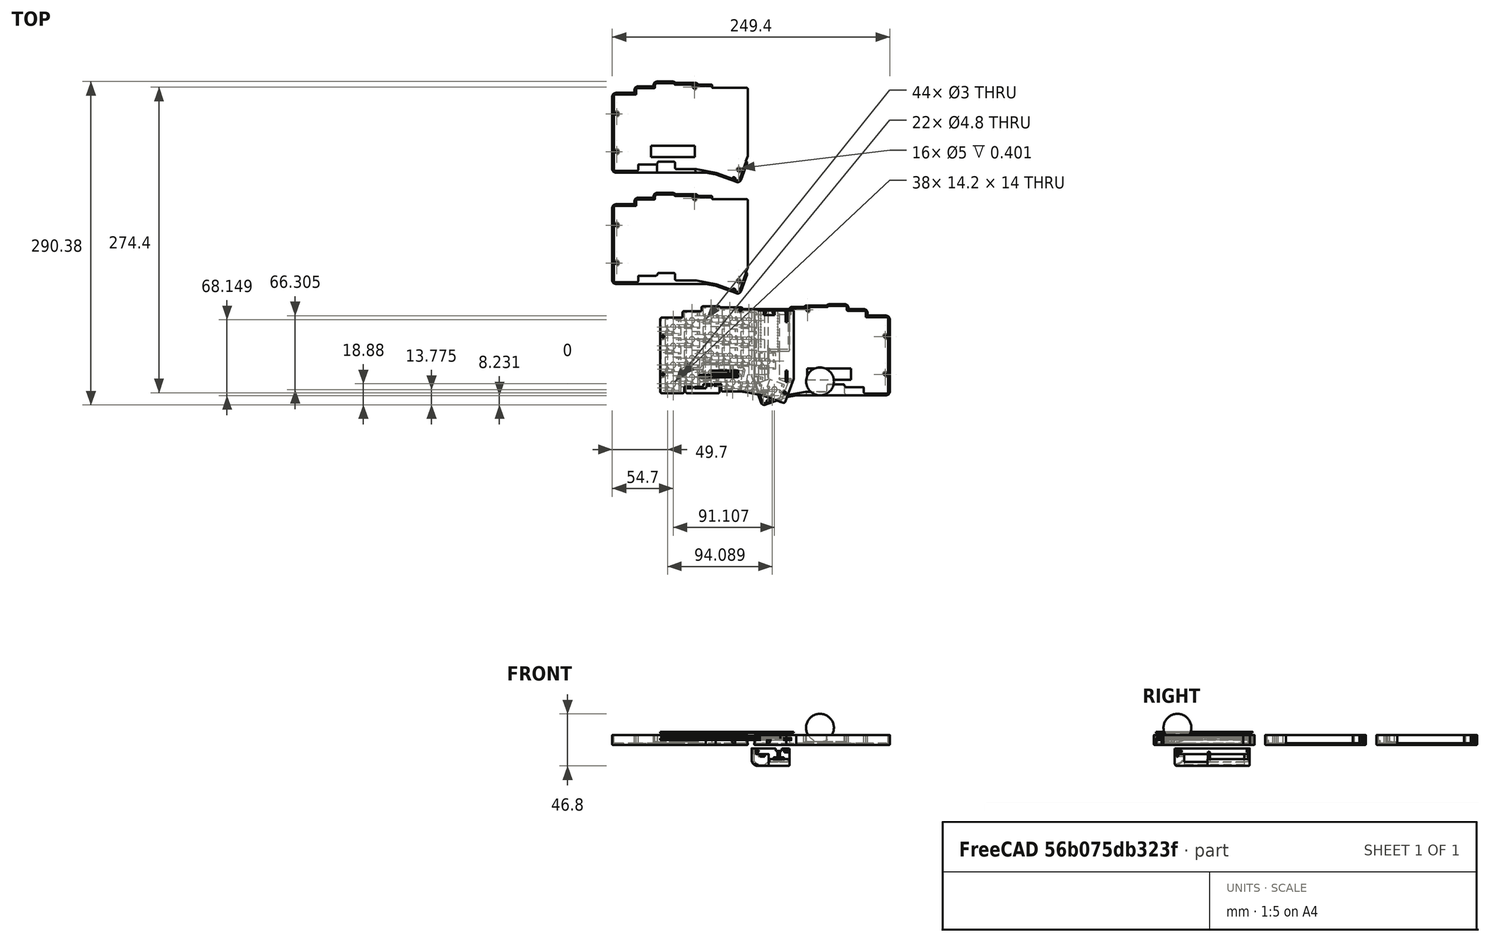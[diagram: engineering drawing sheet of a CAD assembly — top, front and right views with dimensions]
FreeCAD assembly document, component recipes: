
FREECAD ASSEMBLY — COMPONENT RECIPES ("simple-case-xs")

This assembly document has 5 components, labeled P0..P4 below (a component is one placed body or linked part). 4 of them carry a construction recipe — the FreeCAD feature program that regenerates the part from scratch, quoted from this document or its linked companion documents; the rest are supplied as boundary geometry only. No exploded tour is included for this assembly.
NOTE — this tour is split across 3 documents so each fits a 32k-token context. This is document 1: the component sections continue in the remaining 2 documents, each repeating the header above.
COMPONENT P0 — recipe-attached ("Body", modeled in this document).
Construction recipe (the document's own serialized feature program — sketch geometry with constraints, then the solid features built on it; lengths are millimeters unless a unit is written):

FEATURE [Sketcher::SketchObject] Sketch  label="xz"
  ArcFitTolerance = 0
  AttachmentSupport = -> [XZ_Plane]
  FullyConstrained = false
  MakeInternals = false
  MapMode = 5
  Placement = pos=(0,0,0) rot=(1,0,0;1.5708rad)
  expr: Constraints[31] = Spreadsheet.conn_h
  expr: Constraints[57] = Spreadsheet.controller_h
  expr: Constraints[79] = Spreadsheet.battery_h
  sketch-geometry (55):
    g0: LineSegment [constr] StartX=9 StartY=2.5 StartZ=0 EndX=9 EndY=4.1 EndZ=0
    g1: LineSegment [constr] StartX=9 StartY=4.1 StartZ=0 EndX=-9 EndY=4.1 EndZ=0
    g2: LineSegment [constr] StartX=-9 StartY=4.1 StartZ=0 EndX=-9 EndY=2.5 EndZ=0
    g3: LineSegment [constr] StartX=-9 StartY=2.5 StartZ=0 EndX=9 EndY=2.5 EndZ=0
    g4: GeomPoint [constr] X=0 Y=3.3 Z=0
    g5: LineSegment [constr] StartX=-105.409 StartY=0 StartZ=0 EndX=45.7381 EndY=0 EndZ=0
    g6: LineSegment [constr] StartX=45.7381 StartY=0 StartZ=0 EndX=45.7381 EndY=-1.6 EndZ=0
    g7: LineSegment [constr] StartX=45.7381 StartY=-1.6 StartZ=0 EndX=-105.409 EndY=-1.6 EndZ=0
    g8: LineSegment [constr] StartX=-105.409 StartY=-1.6 StartZ=0 EndX=-105.409 EndY=0 EndZ=0
    g9: LineSegment [constr] StartX=9 StartY=2.5 StartZ=0 EndX=6.36312 EndY=2.5 EndZ=0
    g10: LineSegment [constr] StartX=6.36312 StartY=2.5 StartZ=0 EndX=6.36312 EndY=0 EndZ=0
    g11: LineSegment [constr] StartX=6.36312 StartY=0 StartZ=0 EndX=9 EndY=0 EndZ=0
    g12: LineSegment [constr] StartX=9 StartY=0 StartZ=0 EndX=9 EndY=2.5 EndZ=0
    g13: LineSegment [constr] StartX=4.55 StartY=-5.1 StartZ=0 EndX=4.55 EndY=-1.6 EndZ=0
    g14: LineSegment [constr] StartX=4.55 StartY=-1.6 StartZ=0 EndX=-4.55 EndY=-1.6 EndZ=0
    g15: LineSegment [constr] StartX=-4.55 StartY=-1.6 StartZ=0 EndX=-4.55 EndY=-5.1 EndZ=0
    g16: LineSegment [constr] StartX=-4.55 StartY=-5.1 StartZ=0 EndX=4.55 EndY=-5.1 EndZ=0
    g17: GeomPoint [constr] X=0 Y=-3.35 Z=0
    g18: LineSegment [constr] StartX=-4.75 StartY=6.3 StartZ=0 EndX=-4.75 EndY=4.1 EndZ=0
    g19: LineSegment [constr] StartX=-4.75 StartY=4.1 StartZ=0 EndX=4.75 EndY=4.1 EndZ=0
    g20: LineSegment [constr] StartX=4.75 StartY=4.1 StartZ=0 EndX=4.75 EndY=6.3 EndZ=0
    g21: LineSegment [constr] StartX=4.75 StartY=6.3 StartZ=0 EndX=-4.75 EndY=6.3 EndZ=0
    g22: GeomPoint [constr] X=0 Y=5.2 Z=0
    g23: LineSegment [constr] StartX=-44.4822 StartY=-5.1 StartZ=0 EndX=-44.4822 EndY=-3.9 EndZ=0
    g24: LineSegment [constr] StartX=-44.4822 StartY=-3.9 StartZ=0 EndX=44.4822 EndY=-3.9 EndZ=0
    g25: LineSegment [constr] StartX=44.4822 StartY=-3.9 StartZ=0 EndX=44.4822 EndY=-5.1 EndZ=0
    g26: LineSegment [constr] StartX=44.4822 StartY=-5.1 StartZ=0 EndX=-44.4822 EndY=-5.1 EndZ=0
    g27: GeomPoint [constr] X=0 Y=-4.5 Z=0
    g28: LineSegment [constr] StartX=-9.1 StartY=-3.6 StartZ=0 EndX=-9.1 EndY=9.4 EndZ=0
    g29: LineSegment [constr] StartX=-9.1 StartY=9.4 StartZ=0 EndX=-22.1 EndY=9.4 EndZ=0
    g30: LineSegment [constr] StartX=-22.1 StartY=9.4 StartZ=0 EndX=-22.1 EndY=-3.6 EndZ=0
    g31: LineSegment [constr] StartX=-22.1 StartY=-3.6 StartZ=0 EndX=-9.1 EndY=-3.6 EndZ=0
    g32: GeomPoint [constr] X=-15.6 Y=2.9 Z=0
    g33: LineSegment [constr] StartX=33.0788 StartY=0.6 StartZ=0 EndX=33.0788 EndY=2.2 EndZ=0
    g34: LineSegment [constr] StartX=33.0788 StartY=2.2 StartZ=0 EndX=11.9844 EndY=2.2 EndZ=0
    g35: LineSegment [constr] StartX=11.9844 StartY=2.2 StartZ=0 EndX=11.9844 EndY=0.6 EndZ=0
    g36: LineSegment [constr] StartX=11.9844 StartY=0.6 StartZ=0 EndX=33.0788 EndY=0.6 EndZ=0
    g37: GeomPoint [constr] X=22.5316 Y=1.4 Z=0
    g38: LineSegment [constr] StartX=25.7428 StartY=8.6 StartZ=0 EndX=25.7428 EndY=2.2 EndZ=0
    g39: LineSegment [constr] StartX=25.7428 StartY=2.2 StartZ=0 EndX=19.3204 EndY=2.2 EndZ=0
    g40: LineSegment [constr] StartX=19.3204 StartY=2.2 StartZ=0 EndX=19.3204 EndY=8.6 EndZ=0
    g41: LineSegment [constr] StartX=19.3204 StartY=8.6 StartZ=0 EndX=25.7428 EndY=8.6 EndZ=0
    g42: GeomPoint [constr] X=22.5316 Y=5.4 Z=0
    g43: LineSegment [constr] StartX=22.5316 StartY=1.4 StartZ=0 EndX=22.5316 EndY=5.4 EndZ=0
    g44: LineSegment [constr] StartX=29.8817 StartY=5.3 StartZ=0 EndX=29.8817 EndY=0 EndZ=0
    g45: LineSegment [constr] StartX=29.8817 StartY=0 StartZ=0 EndX=15.1815 EndY=0 EndZ=0
    g46: LineSegment [constr] StartX=15.1815 StartY=0 StartZ=0 EndX=15.1815 EndY=5.3 EndZ=0
    g47: LineSegment [constr] StartX=15.1815 StartY=5.3 StartZ=0 EndX=29.8817 EndY=5.3 EndZ=0
    g48: GeomPoint [constr] X=22.5316 Y=2.65 Z=0
    g49: LineSegment [constr] StartX=28.1684 StartY=6.59315 StartZ=0 EndX=28.1684 EndY=9.3 EndZ=0
    g50: LineSegment [constr] StartX=28.1684 StartY=9.3 StartZ=0 EndX=16.8947 EndY=9.3 EndZ=0
    g51: LineSegment [constr] StartX=16.8947 StartY=9.3 StartZ=0 EndX=16.8947 EndY=6.59315 EndZ=0
    g52: LineSegment [constr] StartX=16.8947 StartY=6.59315 StartZ=0 EndX=28.1684 EndY=6.59315 EndZ=0
    g53: GeomPoint [constr] X=22.5316 Y=7.94657 Z=0
    g54: Circle [constr] CenterX=41.3382 CenterY=8.9 CenterZ=0 NormalX=0 NormalY=0 NormalZ=1 AngleXU=0 Radius=12.5
  constraints (135):
    c: Coincident(g0,g1)
    c: Coincident(g1,g2)
    c: Coincident(g2,g3)
    c: Coincident(g3,g0)
    c: Horizontal(g1)
    c: Horizontal(g3)
    c: Vertical(g0)
    c: Vertical(g2)
    c: Symmetric(g1,g0,g4)
    c: PointOnObject(g4,g-2)
    c: Coincident(g5,g6)
    c: Coincident(g6,g7)
    c: Coincident(g7,g8)
    c: Coincident(g8,g5)
    c: Horizontal(g5)
    c: Horizontal(g7)
    c: Vertical(g6)
    c: Vertical(g8)
    c: PointOnObject(g5,g-1)
    c: Distance(g6) = 1.6
    c: Distance(g0) = 1.6
    c: Coincident(g9,g10)
    c: Coincident(g10,g11)
    c: Coincident(g11,g12)
    c: Coincident(g12,g9)
    c: Horizontal(g9)
    c: Horizontal(g11)
    c: Vertical(g10)
    c: Vertical(g12)
    c: Coincident(g9,g0)
    c: PointOnObject(g10,g5)
    c: Distance(g12) = 2.5
    c: Distance(g1) = 18
    c: Coincident(g13,g14)
    c: Coincident(g14,g15)
    c: Coincident(g15,g16)
    c: Coincident(g16,g13)
    c: Horizontal(g14)
    c: Horizontal(g16)
    c: Vertical(g13)
    c: Vertical(g15)
    c: Symmetric(g14,g13,g17)
    c: PointOnObject(g17,g-2)
    c: PointOnObject(g14,g7)
    c: Distance(g13) = 3.5
    c: Distance(g16) = 9.1
    c: Coincident(g18,g19)
    c: Coincident(g19,g20)
    c: Coincident(g20,g21)
    c: Coincident(g21,g18)
    c: Horizontal(g19)
    c: Horizontal(g21)
    c: Vertical(g18)
    c: Vertical(g20)
    c: Symmetric(g19,g18,g22)
    c: PointOnObject(g22,g-2)
    c: PointOnObject(g19,g1)
    c: Distance(g20,g3) = 3.8
    c: Distance(g21) = 9.5
    c: Coincident(g23,g24)
    c: Coincident(g24,g25)
    c: Coincident(g25,g26)
    c: Coincident(g26,g23)
    c: Horizontal(g24)
    c: Horizontal(g26)
    c: Vertical(g23)
    c: Vertical(g25)
    c: Symmetric(g24,g23,g27)
    c: PointOnObject(g27,g-2)
    c: Distance(g25) = 1.2
    c: Coincident(g28,g29)
    c: Coincident(g29,g30)
    c: Coincident(g30,g31)
    c: Coincident(g31,g28)
    c: Horizontal(g29)
    c: Horizontal(g31)
    c: Vertical(g28)
    c: Vertical(g30)
    c: Symmetric(g29,g28,g32)
    c: Distance(g30) = 13
    c: Distance(g29) = 13
    c: Distance(g30,g7) = 2
    c: Distance(g24,g7) = 2.3
    c: Distance(g32,g-2) = 15.6
    c: Coincident(g33,g34)
    c: Coincident(g34,g35)
    c: Coincident(g35,g36)
    c: Coincident(g36,g33)
    c: Horizontal(g34)
    c: Horizontal(g36)
    c: Vertical(g33)
    c: Vertical(g35)
    c: Symmetric(g34,g33,g37)
    c: Distance(g33) = 1.6
    c: Distance(g33,g5) = 0.6
    c: Coincident(g38,g39)
    c: Coincident(g39,g40)
    c: Coincident(g40,g41)
    c: Coincident(g41,g38)
    c: Horizontal(g39)
    c: Horizontal(g41)
    c: Vertical(g38)
    c: Vertical(g40)
    c: Symmetric(g39,g38,g42)
    c: PointOnObject(g39,g34)
    c: Distance(g40) = 6.4
    c: Coincident(g43,g37)
    c: Coincident(g43,g42)
    c: Vertical(g43)
    c: Coincident(g44,g45)
    c: Coincident(g45,g46)
    c: Coincident(g46,g47)
    c: Coincident(g47,g44)
    c: Horizontal(g45)
    c: Horizontal(g47)
    c: Vertical(g44)
    c: Vertical(g46)
    c: Symmetric(g45,g44,g48)
    c: PointOnObject(g48,g43)
    c: PointOnObject(g45,g5)
    c: Distance(g44) = 5.3
    c: Coincident(g49,g50)
    c: Coincident(g50,g51)
    c: Coincident(g51,g52)
    c: Coincident(g52,g49)
    c: Horizontal(g50)
    c: Horizontal(g52)
    c: Vertical(g49)
    c: Vertical(g51)
    c: Symmetric(g50,g49,g53)
    c: PointOnObject(g53,g43)
    c: Distance(g49,g47) = 4
    c: Diameter(g54) = 25
    c: Distance(g54,g24) = 12.8
    c: Distance(g33,g24) = 4.5
FEATURE [Sketcher::SketchObject] Sketch001  label="xy"
  ArcFitTolerance = 0
  AttachmentSupport = -> [XY_Plane]
  FullyConstrained = true
  MakeInternals = false
  MapMode = 5
  expr: Constraints[23] = Spreadsheet.battery_l
  sketch-geometry (20):
    g0: LineSegment [constr] StartX=8.4 StartY=-34 StartZ=0 EndX=8.4 EndY=0 EndZ=0
    g1: LineSegment [constr] StartX=8.4 StartY=0 StartZ=0 EndX=-8.4 EndY=0 EndZ=0
    g2: LineSegment [constr] StartX=-8.4 StartY=0 StartZ=0 EndX=-8.4 EndY=-34 EndZ=0
    g3: LineSegment [constr] StartX=-8.4 StartY=-34 StartZ=0 EndX=8.4 EndY=-34 EndZ=0
    g4: GeomPoint [constr] X=0 Y=-17 Z=0
    g5: LineSegment [constr] StartX=-22.1 StartY=-60.7 StartZ=0 EndX=-22.1 EndY=-3.7 EndZ=0
    g6: LineSegment [constr] StartX=-22.1 StartY=-3.7 StartZ=0 EndX=-9.1 EndY=-3.7 EndZ=0
    g7: LineSegment [constr] StartX=-9.1 StartY=-3.7 StartZ=0 EndX=-9.1 EndY=-60.7 EndZ=0
    g8: LineSegment [constr] StartX=-9.1 StartY=-60.7 StartZ=0 EndX=-22.1 EndY=-60.7 EndZ=0
    g9: GeomPoint [constr] X=-15.6 Y=-32.2 Z=0
    g10: LineSegment [constr] StartX=22.1 StartY=-68.9 StartZ=0 EndX=22.1 EndY=0 EndZ=0
    g11: LineSegment [constr] StartX=22.1 StartY=0 StartZ=0 EndX=-22.1 EndY=0 EndZ=0
    g12: LineSegment [constr] StartX=-22.1 StartY=0 StartZ=0 EndX=-22.1 EndY=-68.9 EndZ=0
    g13: LineSegment [constr] StartX=-22.1 StartY=-68.9 StartZ=0 EndX=22.1 EndY=-68.9 EndZ=0
    g14: GeomPoint [constr] X=0 Y=-34.45 Z=0
    g15: LineSegment [constr] StartX=8.5 StartY=-53.9 StartZ=0 EndX=8.5 EndY=-36.9 EndZ=0
    g16: LineSegment [constr] StartX=8.5 StartY=-36.9 StartZ=0 EndX=-8.5 EndY=-36.9 EndZ=0
    g17: LineSegment [constr] StartX=-8.5 StartY=-36.9 StartZ=0 EndX=-8.5 EndY=-53.9 EndZ=0
    g18: LineSegment [constr] StartX=-8.5 StartY=-53.9 StartZ=0 EndX=8.5 EndY=-53.9 EndZ=0
    g19: GeomPoint [constr] X=0 Y=-45.4 Z=0
  constraints (52):
    c: Coincident(g0,g1)
    c: Coincident(g1,g2)
    c: Coincident(g2,g3)
    c: Coincident(g3,g0)
    c: Horizontal(g1)
    c: Horizontal(g3)
    c: Vertical(g0)
    c: Vertical(g2)
    c: Symmetric(g1,g0,g4)
    c: PointOnObject(g4,g-2)
    c: Distance(g0) = 34
    c: PointOnObject(g-1,g1)
    c: Distance(g3) = 16.8
    c: Coincident(g5,g6)
    c: Coincident(g6,g7)
    c: Coincident(g7,g8)
    c: Coincident(g8,g5)
    c: Horizontal(g6)
    c: Horizontal(g8)
    c: Vertical(g5)
    c: Vertical(g7)
    c: Symmetric(g6,g5,g9)
    c: Distance(g6) = 13
    c: Distance(g5) = 57
    c: Distance(g9,g-1) = 32.2
    c: Coincident(g10,g11)
    c: Coincident(g11,g12)
    c: Coincident(g12,g13)
    c: Coincident(g13,g10)
    c: Horizontal(g11)
    c: Horizontal(g13)
    c: Vertical(g10)
    c: Vertical(g12)
    c: Symmetric(g11,g10,g14)
    c: PointOnObject(g14,g-2)
    c: PointOnObject(g11,g-1)
    c: Distance(g12,g-2) = 22.1
    c: Distance(g10) = 68.9
    c: Coincident(g15,g16)
    c: Coincident(g16,g17)
    c: Coincident(g17,g18)
    c: Coincident(g18,g15)
    c: Horizontal(g16)
    c: Horizontal(g18)
    c: Vertical(g15)
    c: Vertical(g17)
    c: Symmetric(g16,g15,g19)
    c: PointOnObject(g19,g-2)
    c: Distance(g18) = 17
    c: Distance(g15) = 17
    c: Distance(g19,g-1) = 45.4
    c: Distance(g9,g-2) = 15.6
FEATURE [Sketcher::SketchObject] Sketch002
  ArcFitTolerance = 0
  AttachmentOffset = pos=(0,0,10.6) rot=(0,0,1;0rad)
  AttachmentSupport = -> [XY_Plane]
  FullyConstrained = true
  MakeInternals = false
  MapMode = 5
  Placement = pos=(0,0,10.6) rot=(0,0,1;0rad)
  expr: .AttachmentOffset.Base.z = Spreadsheet.battery_h - 3.6 + 1.2
  expr: Constraints[10] = Sketch001.Constraints[10]
  expr: Constraints[12] = Sketch001.Constraints[12]
  expr: Constraints[22] = Sketch001.Constraints[22]
  expr: Constraints[23] = Sketch001.Constraints[23]
  expr: Constraints[24] = Sketch001.Constraints[24]
  expr: Constraints[36] = Sketch001.Constraints[36]
  expr: Constraints[37] = Sketch001.Constraints[37]
  expr: Constraints[48] = Sketch001.Constraints[48]
  expr: Constraints[49] = Sketch001.Constraints[49]
  expr: Constraints[50] = Sketch001.Constraints[50]
  expr: Constraints[51] = Sketch001.Constraints[51]
  sketch-geometry (37):
    g0: LineSegment [constr] StartX=8.4 StartY=-34 StartZ=0 EndX=8.4 EndY=0 EndZ=0
    g1: LineSegment [constr] StartX=8.4 StartY=0 StartZ=0 EndX=-8.4 EndY=0 EndZ=0
    g2: LineSegment [constr] StartX=-8.4 StartY=0 StartZ=0 EndX=-8.4 EndY=-34 EndZ=0
    g3: LineSegment [constr] StartX=-8.4 StartY=-34 StartZ=0 EndX=8.4 EndY=-34 EndZ=0
    g4: GeomPoint [constr] X=0 Y=-17 Z=0
    g5: LineSegment [constr] StartX=-22.1 StartY=-60.7 StartZ=0 EndX=-22.1 EndY=-3.7 EndZ=0
    g6: LineSegment [constr] StartX=-22.1 StartY=-3.7 StartZ=0 EndX=-9.1 EndY=-3.7 EndZ=0
    g7: LineSegment [constr] StartX=-9.1 StartY=-3.7 StartZ=0 EndX=-9.1 EndY=-60.7 EndZ=0
    g8: LineSegment [constr] StartX=-9.1 StartY=-60.7 StartZ=0 EndX=-22.1 EndY=-60.7 EndZ=0
    g9: GeomPoint [constr] X=-15.6 Y=-32.2 Z=0
    g10: LineSegment [constr] StartX=22.1 StartY=-68.9 StartZ=0 EndX=22.1 EndY=0 EndZ=0
    g11: LineSegment [constr] StartX=22.1 StartY=0 StartZ=0 EndX=-22.1 EndY=0 EndZ=0
    g12: LineSegment [constr] StartX=-22.1 StartY=0 StartZ=0 EndX=-22.1 EndY=-68.9 EndZ=0
    g13: LineSegment [constr] StartX=-22.1 StartY=-68.9 StartZ=0 EndX=22.1 EndY=-68.9 EndZ=0
    g14: GeomPoint [constr] X=0 Y=-34.45 Z=0
    g15: LineSegment [constr] StartX=8.5 StartY=-53.9 StartZ=0 EndX=8.5 EndY=-36.9 EndZ=0
    g16: LineSegment [constr] StartX=8.5 StartY=-36.9 StartZ=0 EndX=-8.5 EndY=-36.9 EndZ=0
    g17: LineSegment [constr] StartX=-8.5 StartY=-36.9 StartZ=0 EndX=-8.5 EndY=-53.9 EndZ=0
    g18: LineSegment [constr] StartX=-8.5 StartY=-53.9 StartZ=0 EndX=8.5 EndY=-53.9 EndZ=0
    g19: GeomPoint [constr] X=0 Y=-45.4 Z=0
    g20: LineSegment StartX=9.6 StartY=1.3 StartZ=0 EndX=-24.5 EndY=1.3 EndZ=0
    g21: LineSegment StartX=-24.5 StartY=1.3 StartZ=0 EndX=-24.5 EndY=-1.7 EndZ=0
    g22: LineSegment StartX=-24.5 StartY=-1.7 StartZ=0 EndX=-24.5 EndY=-1.7 EndZ=0
    g23: LineSegment StartX=-24.5 StartY=-1.7 StartZ=0 EndX=-24.5 EndY=-58.7602 EndZ=0
    g24: LineSegment [constr] StartX=-9.1 StartY=-61.6 StartZ=0 EndX=-9.1 EndY=-36.6 EndZ=0
    g25: LineSegment [constr] StartX=-21.7859 StartY=-66.2173 StartZ=0 EndX=-9.1 EndY=-61.6 EndZ=0
    g26: LineSegment StartX=-9.1 StartY=-36.6 StartZ=0 EndX=9.6 EndY=-36.6 EndZ=0
    g27: LineSegment StartX=9.6 StartY=-36.6 StartZ=0 EndX=9.6 EndY=1.3 EndZ=0
    g28: LineSegment StartX=-24.5 StartY=-58.7602 StartZ=0 EndX=-21.7859 EndY=-66.2173 EndZ=0
    g29: LineSegment [constr] StartX=26.9 StartY=-17.32 StartZ=0 EndX=26.9 EndY=-0.32 EndZ=0
    g30: LineSegment [constr] StartX=26.9 StartY=-0.32 StartZ=0 EndX=9.9 EndY=-0.32 EndZ=0
    g31: LineSegment [constr] StartX=9.9 StartY=-0.32 StartZ=0 EndX=9.9 EndY=-17.32 EndZ=0
    g32: LineSegment [constr] StartX=9.9 StartY=-17.32 StartZ=0 EndX=26.9 EndY=-17.32 EndZ=0
    g33: GeomPoint [constr] X=18.4 Y=-8.82 Z=0
    g34: LineSegment StartX=-9.1 StartY=-36.6 StartZ=0 EndX=-9.25 EndY=-36.6 EndZ=0
    g35: LineSegment StartX=-9.25 StartY=-36.6 StartZ=0 EndX=-9.25 EndY=-61.6546 EndZ=0
    g36: LineSegment StartX=-9.25 StartY=-61.6546 StartZ=0 EndX=-21.7859 EndY=-66.2173 EndZ=0
  constraints (100):
    c: Coincident(g0,g1)
    c: Coincident(g1,g2)
    c: Coincident(g2,g3)
    c: Coincident(g3,g0)
    c: Horizontal(g1)
    c: Horizontal(g3)
    c: Vertical(g0)
    c: Vertical(g2)
    c: Symmetric(g1,g0,g4)
    c: PointOnObject(g4,g-2)
    c: Distance(g0) = 34
    c: PointOnObject(g-1,g1)
    c: Distance(g3) = 16.8
    c: Coincident(g5,g6)
    c: Coincident(g6,g7)
    c: Coincident(g7,g8)
    c: Coincident(g8,g5)
    c: Horizontal(g6)
    c: Horizontal(g8)
    c: Vertical(g5)
    c: Vertical(g7)
    c: Symmetric(g6,g5,g9)
    c: Distance(g6) = 13
    c: Distance(g5) = 57
    c: Distance(g9,g-1) = 32.2
    c: Coincident(g10,g11)
    c: Coincident(g11,g12)
    c: Coincident(g12,g13)
    c: Coincident(g13,g10)
    c: Horizontal(g11)
    c: Horizontal(g13)
    c: Vertical(g10)
    c: Vertical(g12)
    c: Symmetric(g11,g10,g14)
    c: PointOnObject(g14,g-2)
    c: PointOnObject(g11,g-1)
    c: Distance(g12,g-2) = 22.1
    c: Distance(g10) = 68.9
    c: Coincident(g15,g16)
    c: Coincident(g16,g17)
    c: Coincident(g17,g18)
    c: Coincident(g18,g15)
    c: Horizontal(g16)
    c: Horizontal(g18)
    c: Vertical(g15)
    c: Vertical(g17)
    c: Symmetric(g16,g15,g19)
    c: PointOnObject(g19,g-2)
    c: Distance(g18) = 17
    c: Distance(g15) = 17
    c: Distance(g19,g-1) = 45.4
    c: Distance(g9,g-2) = 15.6
    c: Horizontal(g20)
    c: Coincident(g21,g20)
    c: Vertical(g21)
    c: Coincident(g22,g21)
    c: Horizontal(g22)
    c: Coincident(g23,g22)
    c: Vertical(g23)
    c: PointOnObject(g24,g7)
    c: Vertical(g24)
    c: Distance(g11,g21) = 2.4
    c: Distance(g21,g6) = 2
    c: Distance(g22,g5) = 2.4
    c: Coincident(g24,g25)
    c: Angle(g13,g25) = 0.349066
    c: DistanceY(g-1,g20) = 1.3
    c: Coincident(g26,g24)
    c: Horizontal(g26)
    c: Coincident(g27,g26)
    c: Coincident(g27,g20)
    c: Vertical(g27)
    c: Distance(g15,g26) = 0.3
    c: Coincident(g28,g23)
    c: Coincident(g28,g25)
    c: Distance(g25,g25) = 13.5
    c: Perpendicular(g28,g25)
    c: Distance(g24,g8) = 0.9
    c: Coincident(g29,g30)
    c: Coincident(g30,g31)
    c: Coincident(g31,g32)
    c: Coincident(g32,g29)
    c: Vertical(g29)
    c: Vertical(g31)
    c: Horizontal(g30)
    c: Horizontal(g32)
    c: Symmetric(g31,g29,g33)
    c: DistanceX(g30,g30) = 17
    c: DistanceY(g29,g29) = 17
    c: DistanceX(g-1,g33) = 18.4
    c: DistanceY(g33,g-1) = 8.82
    c: Distance(g31,g27) = 0.3
    c: Coincident(g24,g34)
    c: Horizontal(g34)
    c: Coincident(g34,g35)
    c: PointOnObject(g35,g25)
    c: Vertical(g35)
    c: Coincident(g35,g36)
    c: Coincident(g36,g25)
    c: Distance(g35,g7) = 0.15
FEATURE [PartDesign::Pad] Pad  label="ベース"
  Direction = (0,0,1)
  Length = 15.7
  Length2 = 10
  Profile = -> Sketch002
  ReferenceAxis = -> Sketch002 [N_Axis]
  Reversed = true
  Suppressed = false
  Type = 0
  expr: Length = Spreadsheet.battery_h + 1.2 + 0.3 + 1.2
FEATURE [Sketcher::SketchObject] Sketch003
  ArcFitTolerance = 0
  AttachmentOffset = pos=(0,0,6.9) rot=(0,0,1;0rad)
  AttachmentSupport = -> [XY_Plane]
  FullyConstrained = false
  MakeInternals = false
  MapMode = 5
  Placement = pos=(0,0,6.9) rot=(0,0,1;0rad)
  expr: .AttachmentOffset.Base.z = Spreadsheet.conn_h + Spreadsheet.controller_h + 0.6
  expr: Constraints[10] = Sketch001.Constraints[10]
  expr: Constraints[12] = Sketch001.Constraints[12]
  expr: Constraints[22] = Sketch001.Constraints[22]
  expr: Constraints[23] = Sketch001.Constraints[23]
  expr: Constraints[24] = Sketch001.Constraints[24]
  expr: Constraints[36] = Sketch001.Constraints[36]
  expr: Constraints[37] = Sketch001.Constraints[37]
  expr: Constraints[48] = Sketch001.Constraints[48]
  expr: Constraints[49] = Sketch001.Constraints[49]
  expr: Constraints[50] = Sketch001.Constraints[50]
  expr: Constraints[51] = Sketch001.Constraints[51]
  sketch-geometry (24):
    g0: LineSegment [constr] StartX=8.4 StartY=-34 StartZ=0 EndX=8.4 EndY=0 EndZ=0
    g1: LineSegment [constr] StartX=8.4 StartY=0 StartZ=0 EndX=-8.4 EndY=0 EndZ=0
    g2: LineSegment [constr] StartX=-8.4 StartY=0 StartZ=0 EndX=-8.4 EndY=-34 EndZ=0
    g3: LineSegment [constr] StartX=-8.4 StartY=-34 StartZ=0 EndX=8.4 EndY=-34 EndZ=0
    g4: GeomPoint [constr] X=0 Y=-17 Z=0
    g5: LineSegment [constr] StartX=-22.1 StartY=-60.7 StartZ=0 EndX=-22.1 EndY=-3.7 EndZ=0
    g6: LineSegment [constr] StartX=-22.1 StartY=-3.7 StartZ=0 EndX=-9.1 EndY=-3.7 EndZ=0
    g7: LineSegment [constr] StartX=-9.1 StartY=-3.7 StartZ=0 EndX=-9.1 EndY=-60.7 EndZ=0
    g8: LineSegment [constr] StartX=-9.1 StartY=-60.7 StartZ=0 EndX=-22.1 EndY=-60.7 EndZ=0
    g9: GeomPoint [constr] X=-15.6 Y=-32.2 Z=0
    g10: LineSegment [constr] StartX=22.1 StartY=-68.9 StartZ=0 EndX=22.1 EndY=0 EndZ=0
    g11: LineSegment [constr] StartX=22.1 StartY=0 StartZ=0 EndX=-22.1 EndY=0 EndZ=0
    g12: LineSegment [constr] StartX=-22.1 StartY=0 StartZ=0 EndX=-22.1 EndY=-68.9 EndZ=0
    g13: LineSegment [constr] StartX=-22.1 StartY=-68.9 StartZ=0 EndX=22.1 EndY=-68.9 EndZ=0
    g14: GeomPoint [constr] X=0 Y=-34.45 Z=0
    g15: LineSegment [constr] StartX=8.5 StartY=-53.9 StartZ=0 EndX=8.5 EndY=-36.9 EndZ=0
    g16: LineSegment [constr] StartX=8.5 StartY=-36.9 StartZ=0 EndX=-8.5 EndY=-36.9 EndZ=0
    g17: LineSegment [constr] StartX=-8.5 StartY=-36.9 StartZ=0 EndX=-8.5 EndY=-53.9 EndZ=0
    g18: LineSegment [constr] StartX=-8.5 StartY=-53.9 StartZ=0 EndX=8.5 EndY=-53.9 EndZ=0
    g19: GeomPoint [constr] X=0 Y=-45.4 Z=0
    g20: LineSegment StartX=8.4 StartY=0 StartZ=0 EndX=-9.1 EndY=0 EndZ=0
    g21: LineSegment StartX=-9.1 StartY=0 StartZ=0 EndX=-9.1 EndY=-40.6656 EndZ=0
    g22: LineSegment StartX=-9.1 StartY=-40.6656 StartZ=0 EndX=8.4 EndY=-40.6656 EndZ=0
    g23: LineSegment StartX=8.4 StartY=-40.6656 StartZ=0 EndX=8.4 EndY=0 EndZ=0
  constraints (62):
    c: Coincident(g0,g1)
    c: Coincident(g1,g2)
    c: Coincident(g2,g3)
    c: Coincident(g3,g0)
    c: Horizontal(g1)
    c: Horizontal(g3)
    c: Vertical(g0)
    c: Vertical(g2)
    c: Symmetric(g1,g0,g4)
    c: PointOnObject(g4,g-2)
    c: Distance(g0) = 34
    c: PointOnObject(g-1,g1)
    c: Distance(g3) = 16.8
    c: Coincident(g5,g6)
    c: Coincident(g6,g7)
    c: Coincident(g7,g8)
    c: Coincident(g8,g5)
    c: Horizontal(g6)
    c: Horizontal(g8)
    c: Vertical(g5)
    c: Vertical(g7)
    c: Symmetric(g6,g5,g9)
    c: Distance(g6) = 13
    c: Distance(g5) = 57
    c: Distance(g9,g-1) = 32.2
    c: Coincident(g10,g11)
    c: Coincident(g11,g12)
    c: Coincident(g12,g13)
    c: Coincident(g13,g10)
    c: Horizontal(g11)
    c: Horizontal(g13)
    c: Vertical(g10)
    c: Vertical(g12)
    c: Symmetric(g11,g10,g14)
    c: PointOnObject(g14,g-2)
    c: PointOnObject(g11,g-1)
    c: Distance(g12,g-2) = 22.1
    c: Distance(g10) = 68.9
    c: Coincident(g15,g16)
    c: Coincident(g16,g17)
    c: Coincident(g17,g18)
    c: Coincident(g18,g15)
    c: Horizontal(g16)
    c: Horizontal(g18)
    c: Vertical(g15)
    c: Vertical(g17)
    c: Symmetric(g16,g15,g19)
    c: PointOnObject(g19,g-2)
    c: Distance(g18) = 17
    c: Distance(g15) = 17
    c: Distance(g19,g-1) = 45.4
    c: Distance(g9,g-2) = 15.6
    c: Coincident(g20,g21)
    c: Coincident(g21,g22)
    c: Coincident(g22,g23)
    c: Coincident(g23,g20)
    c: Horizontal(g20)
    c: Horizontal(g22)
    c: Vertical(g21)
    c: Vertical(g23)
    c: Coincident(g20,g0)
    c: PointOnObject(g21,g7)
FEATURE [PartDesign::Pocket] Pocket  label="コントローラ部"
  BaseFeature = -> Pad
  Direction = (0,0,-1)
  Length = 5
  Length2 = 5
  Profile = -> Sketch003
  ReferenceAxis = -> Sketch003 [N_Axis]
  Suppressed = false
  Type = 1
FEATURE [Sketcher::SketchObject] Sketch007
  ArcFitTolerance = 0
  AttachmentSupport = -> [XY_Plane]
  FullyConstrained = false
  MakeInternals = false
  MapMode = 5
  expr: Constraints[10] = Sketch001.Constraints[10]
  expr: Constraints[12] = Sketch001.Constraints[12]
  expr: Constraints[21] = Sketch001.Constraints[22]
  expr: Constraints[22] = Sketch001.Constraints[23]
  expr: Constraints[23] = Sketch001.Constraints[24]
  expr: Constraints[35] = Sketch001.Constraints[36]
  expr: Constraints[36] = Sketch001.Constraints[37]
  expr: Constraints[47] = Sketch001.Constraints[48]
  expr: Constraints[48] = Sketch001.Constraints[49]
  expr: Constraints[49] = Sketch001.Constraints[50]
  expr: Constraints[50] = Sketch001.Constraints[51]
  sketch-geometry (28):
    g0: LineSegment [constr] StartX=8.4 StartY=-34 StartZ=0 EndX=8.4 EndY=0 EndZ=0
    g1: LineSegment [constr] StartX=8.4 StartY=0 StartZ=0 EndX=-8.4 EndY=0 EndZ=0
    g2: LineSegment [constr] StartX=-8.4 StartY=0 StartZ=0 EndX=-8.4 EndY=-34 EndZ=0
    g3: LineSegment [constr] StartX=-8.4 StartY=-34 StartZ=0 EndX=8.4 EndY=-34 EndZ=0
    g4: GeomPoint [constr] X=0 Y=-17 Z=0
    g5: LineSegment [constr] StartX=-22.1 StartY=-60.7 StartZ=0 EndX=-22.1 EndY=-3.7 EndZ=0
    g6: LineSegment [constr] StartX=-22.1 StartY=-3.7 StartZ=0 EndX=-9.1 EndY=-3.7 EndZ=0
    g7: LineSegment [constr] StartX=-9.1 StartY=-3.7 StartZ=0 EndX=-9.1 EndY=-60.7 EndZ=0
    g8: LineSegment [constr] StartX=-9.1 StartY=-60.7 StartZ=0 EndX=-22.1 EndY=-60.7 EndZ=0
    g9: GeomPoint [constr] X=-15.6 Y=-32.2 Z=0
    g10: LineSegment [constr] StartX=22.1 StartY=-68.9 StartZ=0 EndX=22.1 EndY=0 EndZ=0
    g11: LineSegment [constr] StartX=22.1 StartY=0 StartZ=0 EndX=-22.1 EndY=0 EndZ=0
    g12: LineSegment [constr] StartX=-22.1 StartY=0 StartZ=0 EndX=-22.1 EndY=-68.9 EndZ=0
    g13: LineSegment [constr] StartX=-22.1 StartY=-68.9 StartZ=0 EndX=22.1 EndY=-68.9 EndZ=0
    g14: GeomPoint [constr] X=0 Y=-34.45 Z=0
    g15: LineSegment [constr] StartX=8.5 StartY=-53.9 StartZ=0 EndX=8.5 EndY=-36.9 EndZ=0
    g16: LineSegment [constr] StartX=8.5 StartY=-36.9 StartZ=0 EndX=-8.5 EndY=-36.9 EndZ=0
    g17: LineSegment [constr] StartX=-8.5 StartY=-36.9 StartZ=0 EndX=-8.5 EndY=-53.9 EndZ=0
    g18: LineSegment [constr] StartX=-8.5 StartY=-53.9 StartZ=0 EndX=8.5 EndY=-53.9 EndZ=0
    g19: GeomPoint [constr] X=-1.4e-15 Y=-45.4 Z=0
    g20: LineSegment StartX=22.1 StartY=0 StartZ=0 EndX=-22.4 EndY=0 EndZ=0
    g21: LineSegment StartX=-22.4 StartY=0 StartZ=0 EndX=-22.4 EndY=-4 EndZ=0
    g22: LineSegment StartX=-22.4 StartY=-4 StartZ=0 EndX=-22.4 EndY=-60.9323 EndZ=0
    g23: LineSegment [constr] StartX=-22.4 StartY=-60.4 StartZ=0 EndX=-22.4 EndY=-68.9 EndZ=0
    g24: LineSegment [constr] StartX=-22.4 StartY=-68.9 StartZ=0 EndX=22.1 EndY=-68.9 EndZ=0
    g25: LineSegment StartX=22.1 StartY=-68.9 StartZ=0 EndX=22.1 EndY=0 EndZ=0
    g26: LineSegment StartX=-19.5 StartY=-68.9 StartZ=0 EndX=22.1 EndY=-68.9 EndZ=0
    g27: LineSegment StartX=-22.4 StartY=-60.9323 StartZ=0 EndX=-19.5 EndY=-68.9 EndZ=0
  constraints (71):
    c: Coincident(g0,g1)
    c: Coincident(g1,g2)
    c: Coincident(g2,g3)
    c: Coincident(g3,g0)
    c: Horizontal(g1)
    c: Horizontal(g3)
    c: Vertical(g0)
    c: Vertical(g2)
    c: Symmetric(g1,g0,g4)
    c: PointOnObject(g4,g-2)
    c: Distance(g0) = 34
    c: PointOnObject(g-1,g1)
    c: Distance(g3) = 16.8
    c: Coincident(g5,g6)
    c: Coincident(g6,g7)
    c: Coincident(g7,g8)
    c: Horizontal(g6)
    c: Horizontal(g8)
    c: Vertical(g5)
    c: Vertical(g7)
    c: Symmetric(g6,g5,g9)
    c: Distance(g6) = 13
    c: Distance(g5) = 57
    c: Distance(g9,g-1) = 32.2
    c: Coincident(g10,g11)
    c: Coincident(g11,g12)
    c: Coincident(g12,g13)
    c: Coincident(g13,g10)
    c: Horizontal(g11)
    c: Horizontal(g13)
    c: Vertical(g10)
    c: Vertical(g12)
    c: Symmetric(g11,g10,g14)
    c: PointOnObject(g14,g-2)
    c: PointOnObject(g11,g-1)
    c: Distance(g12,g-2) = 22.1
    c: Distance(g10) = 68.9
    c: Coincident(g15,g16)
    c: Coincident(g16,g17)
    c: Coincident(g17,g18)
    c: Coincident(g18,g15)
    c: Horizontal(g16)
    c: Horizontal(g18)
    c: Vertical(g15)
    c: Vertical(g17)
    c: Symmetric(g16,g15,g19)
    c: PointOnObject(g19,g-2)
    c: Distance(g18) = 17
    c: Distance(g15) = 17
    c: Distance(g19,g-1) = 45.4
    c: Distance(g9,g-2) = 15.6
    c: Coincident(g20,g10)
    c: PointOnObject(g20,g-1)
    c: Coincident(g21,g20)
    c: Vertical(g21)
    c: Vertical(g22)
    c: Vertical(g23)
    c: Coincident(g24,g23)
    c: Coincident(g24,g10)
    c: Horizontal(g24)
    c: Coincident(g25,g24)
    c: Coincident(g25,g20)
    c: Distance(g21,g12) = 0.3
    c: Distance(g21,g6) = 0.3
    c: PointOnObject(g26,g13)
    c: Coincident(g26,g10)
    c: Coincident(g27,g22)
    c: Coincident(g27,g26)
    c: Angle(g26,g27) = 1.91986
    c: DistanceX(g27,g27) = 2.9
    c: Coincident(g22,g21)
FEATURE [PartDesign::Pocket] Pocket001  label="基板部"
  BaseFeature = -> Pocket
  Direction = (0,0,-1)
  Length = 5
  Length2 = 5
  Profile = -> Sketch007
  ReferenceAxis = -> Sketch007 [N_Axis]
  Suppressed = false
  Type = 1
FEATURE [Sketcher::SketchObject] Sketch008
  ArcFitTolerance = 0
  AttachmentOffset = pos=(0,0,3.4) rot=(0,0,1;0rad)
  AttachmentSupport = -> [XZ_Plane]
  FullyConstrained = false
  MakeInternals = false
  MapMode = 5
  Placement = pos=(0,-3.4,8e-16) rot=(1,0,0;1.5708rad)
  expr: Constraints[105] = Sketch.Constraints[105]
  expr: Constraints[120] = Sketch.Constraints[120]
  expr: Constraints[131] = Sketch.Constraints[131]
  expr: Constraints[132] = Sketch.Constraints[132]
  expr: Constraints[133] = Sketch.Constraints[133]
  expr: Constraints[19] = Sketch.Constraints[19]
  expr: Constraints[20] = Sketch.Constraints[20]
  expr: Constraints[31] = Sketch.Constraints[31]
  expr: Constraints[32] = Sketch.Constraints[32]
  expr: Constraints[44] = Sketch.Constraints[44]
  expr: Constraints[45] = Sketch.Constraints[45]
  expr: Constraints[57] = Sketch.Constraints[57]
  expr: Constraints[58] = Sketch.Constraints[58]
  expr: Constraints[69] = Sketch.Constraints[69]
  expr: Constraints[79] = Sketch.Constraints[79]
  expr: Constraints[80] = Sketch.Constraints[80]
  expr: Constraints[81] = Sketch.Constraints[81]
  expr: Constraints[82] = Sketch.Constraints[82]
  expr: Constraints[83] = Sketch.Constraints[83]
  expr: Constraints[93] = Sketch.Constraints[93]
  expr: Constraints[94] = Sketch.Constraints[94]
  sketch-geometry (70):
    g0: LineSegment [constr] StartX=9 StartY=2.5 StartZ=0 EndX=9 EndY=4.1 EndZ=0
    g1: LineSegment [constr] StartX=9 StartY=4.1 StartZ=0 EndX=-9 EndY=4.1 EndZ=0
    g2: LineSegment [constr] StartX=-9 StartY=4.1 StartZ=0 EndX=-9 EndY=2.5 EndZ=0
    g3: LineSegment [constr] StartX=-9 StartY=2.5 StartZ=0 EndX=9 EndY=2.5 EndZ=0
    g4: GeomPoint [constr] X=0 Y=3.3 Z=0
    g5: LineSegment [constr] StartX=-105.409 StartY=0 StartZ=0 EndX=45.7381 EndY=0 EndZ=0
    g6: LineSegment [constr] StartX=45.7381 StartY=0 StartZ=0 EndX=45.7381 EndY=-1.6 EndZ=0
    g7: LineSegment [constr] StartX=45.7381 StartY=-1.6 StartZ=0 EndX=-105.409 EndY=-1.6 EndZ=0
    g8: LineSegment [constr] StartX=-105.409 StartY=-1.6 StartZ=0 EndX=-105.409 EndY=0 EndZ=0
    g9: LineSegment [constr] StartX=9 StartY=2.5 StartZ=0 EndX=6.36312 EndY=2.5 EndZ=0
    g10: LineSegment [constr] StartX=6.36312 StartY=2.5 StartZ=0 EndX=6.36312 EndY=0 EndZ=0
    g11: LineSegment [constr] StartX=6.36312 StartY=0 StartZ=0 EndX=9 EndY=0 EndZ=0
    g12: LineSegment [constr] StartX=9 StartY=0 StartZ=0 EndX=9 EndY=2.5 EndZ=0
    g13: LineSegment [constr] StartX=4.55 StartY=-5.1 StartZ=0 EndX=4.55 EndY=-1.6 EndZ=0
    g14: LineSegment [constr] StartX=4.55 StartY=-1.6 StartZ=0 EndX=-4.55 EndY=-1.6 EndZ=0
    g15: LineSegment [constr] StartX=-4.55 StartY=-1.6 StartZ=0 EndX=-4.55 EndY=-5.1 EndZ=0
    g16: LineSegment [constr] StartX=-4.55 StartY=-5.1 StartZ=0 EndX=4.55 EndY=-5.1 EndZ=0
    g17: GeomPoint [constr] X=0 Y=-3.35 Z=0
    g18: LineSegment [constr] StartX=-4.75 StartY=6.3 StartZ=0 EndX=-4.75 EndY=4.1 EndZ=0
    g19: LineSegment [constr] StartX=-4.75 StartY=4.1 StartZ=0 EndX=4.75 EndY=4.1 EndZ=0
    g20: LineSegment [constr] StartX=4.75 StartY=4.1 StartZ=0 EndX=4.75 EndY=6.3 EndZ=0
    g21: LineSegment [constr] StartX=4.75 StartY=6.3 StartZ=0 EndX=-4.75 EndY=6.3 EndZ=0
    g22: GeomPoint [constr] X=0 Y=5.2 Z=0
    g23: LineSegment [constr] StartX=-44.4822 StartY=-5.1 StartZ=0 EndX=-44.4822 EndY=-3.9 EndZ=0
    g24: LineSegment [constr] StartX=-44.4822 StartY=-3.9 StartZ=0 EndX=44.4822 EndY=-3.9 EndZ=0
    g25: LineSegment [constr] StartX=44.4822 StartY=-3.9 StartZ=0 EndX=44.4822 EndY=-5.1 EndZ=0
    g26: LineSegment [constr] StartX=44.4822 StartY=-5.1 StartZ=0 EndX=-44.4822 EndY=-5.1 EndZ=0
    g27: GeomPoint [constr] X=0 Y=-4.5 Z=0
    g28: LineSegment [constr] StartX=-9.1 StartY=-3.6 StartZ=0 EndX=-9.1 EndY=9.4 EndZ=0
    g29: LineSegment [constr] StartX=-9.1 StartY=9.4 StartZ=0 EndX=-22.1 EndY=9.4 EndZ=0
    g30: LineSegment [constr] StartX=-22.1 StartY=9.4 StartZ=0 EndX=-22.1 EndY=-3.6 EndZ=0
    g31: LineSegment [constr] StartX=-22.1 StartY=-3.6 StartZ=0 EndX=-9.1 EndY=-3.6 EndZ=0
    g32: GeomPoint [constr] X=-15.6 Y=2.9 Z=0
    g33: LineSegment [constr] StartX=33.0788 StartY=0.6 StartZ=0 EndX=33.0788 EndY=2.2 EndZ=0
    g34: LineSegment [constr] StartX=33.0788 StartY=2.2 StartZ=0 EndX=11.9844 EndY=2.2 EndZ=0
    g35: LineSegment [constr] StartX=11.9844 StartY=2.2 StartZ=0 EndX=11.9844 EndY=0.6 EndZ=0
    g36: LineSegment [constr] StartX=11.9844 StartY=0.6 StartZ=0 EndX=33.0788 EndY=0.6 EndZ=0
    g37: GeomPoint [constr] X=22.5316 Y=1.4 Z=0
    g38: LineSegment [constr] StartX=25.7428 StartY=8.6 StartZ=0 EndX=25.7428 EndY=2.2 EndZ=0
    g39: LineSegment [constr] StartX=25.7428 StartY=2.2 StartZ=0 EndX=19.3204 EndY=2.2 EndZ=0
    g40: LineSegment [constr] StartX=19.3204 StartY=2.2 StartZ=0 EndX=19.3204 EndY=8.6 EndZ=0
    g41: LineSegment [constr] StartX=19.3204 StartY=8.6 StartZ=0 EndX=25.7428 EndY=8.6 EndZ=0
    g42: GeomPoint [constr] X=22.5316 Y=5.4 Z=0
    g43: LineSegment [constr] StartX=22.5316 StartY=1.4 StartZ=0 EndX=22.5316 EndY=5.4 EndZ=0
    g44: LineSegment [constr] StartX=29.8817 StartY=5.3 StartZ=0 EndX=29.8817 EndY=0 EndZ=0
    g45: LineSegment [constr] StartX=29.8817 StartY=0 StartZ=0 EndX=15.1815 EndY=0 EndZ=0
    g46: LineSegment [constr] StartX=15.1815 StartY=0 StartZ=0 EndX=15.1815 EndY=5.3 EndZ=0
    g47: LineSegment [constr] StartX=15.1815 StartY=5.3 StartZ=0 EndX=29.8817 EndY=5.3 EndZ=0
    g48: GeomPoint [constr] X=22.5316 Y=2.65 Z=0
    g49: LineSegment [constr] StartX=28.1684 StartY=6.59315 StartZ=0 EndX=28.1684 EndY=9.3 EndZ=0
    g50: LineSegment [constr] StartX=28.1684 StartY=9.3 StartZ=0 EndX=16.8947 EndY=9.3 EndZ=0
    g51: LineSegment [constr] StartX=16.8947 StartY=9.3 StartZ=0 EndX=16.8947 EndY=6.59315 EndZ=0
    g52: LineSegment [constr] StartX=16.8947 StartY=6.59315 StartZ=0 EndX=28.1684 EndY=6.59315 EndZ=0
    g53: GeomPoint [constr] X=22.5316 Y=7.94657 Z=0
    g54: Circle [constr] CenterX=41.3382 CenterY=8.9 CenterZ=0 NormalX=0 NormalY=0 NormalZ=1 AngleXU=0 Radius=12.5
    g55: GeomPoint [constr] X=-15.6 Y=2.9 Z=0
    g56: LineSegment [constr] StartX=-15.6 StartY=2.9 StartZ=0 EndX=-15.6 EndY=9.4 EndZ=0
    g57: Circle [constr] CenterX=-15.6 CenterY=2.9 CenterZ=0 NormalX=0 NormalY=0 NormalZ=1 AngleXU=0 Radius=6.5
    g58: LineSegment [constr] StartX=-26.7128 StartY=2.9 StartZ=0 EndX=-11.1456 EndY=2.9 EndZ=0
    g59: ArcOfCircle [constr] CenterX=-15.6 CenterY=2.9 CenterZ=0 NormalX=0 NormalY=0 NormalZ=1 AngleXU=0 Radius=7 StartAngle=0 EndAngle=3.14159
    g60: LineSegment [constr] StartX=-21.3446 StartY=6.9 StartZ=0 EndX=-9.85544 EndY=6.9 EndZ=0
    g61: LineSegment [constr] StartX=-18.1981 StartY=9.4 StartZ=0 EndX=-13.0019 EndY=9.4 EndZ=0
    g62: ArcOfCircle CenterX=-15.6 CenterY=2.9 CenterZ=0 NormalX=0 NormalY=0 NormalZ=1 AngleXU=0 Radius=7 StartAngle=0.608246 EndAngle=1.19055
    g63: ArcOfCircle CenterX=-15.6 CenterY=2.9 CenterZ=0 NormalX=0 NormalY=0 NormalZ=1 AngleXU=0 Radius=7 StartAngle=1.95105 EndAngle=2.53335
    g64: LineSegment StartX=-18.1981 StartY=9.4 StartZ=0 EndX=-13.0019 EndY=9.4 EndZ=0
    g65: LineSegment StartX=-21.3446 StartY=6.9 StartZ=0 EndX=-22.1 EndY=6.9 EndZ=0
    g66: LineSegment StartX=-22.1 StartY=6.9 StartZ=0 EndX=-22.1 EndY=-3.6 EndZ=0
    g67: LineSegment StartX=-22.1 StartY=-3.6 StartZ=0 EndX=-9.1 EndY=-3.6 EndZ=0
    g68: LineSegment StartX=-9.85544 StartY=6.9 StartZ=0 EndX=-9.1 EndY=6.9 EndZ=0
    g69: LineSegment StartX=-9.1 StartY=6.9 StartZ=0 EndX=-9.1 EndY=-3.6 EndZ=0
  constraints (176):
    c: Coincident(g0,g1)
    c: Coincident(g1,g2)
    c: Coincident(g2,g3)
    c: Coincident(g3,g0)
    c: Horizontal(g1)
    c: Horizontal(g3)
    c: Vertical(g0)
    c: Vertical(g2)
    c: Symmetric(g1,g0,g4)
    c: PointOnObject(g4,g-2)
    c: Coincident(g5,g6)
    c: Coincident(g6,g7)
    c: Coincident(g7,g8)
    c: Coincident(g8,g5)
    c: Horizontal(g5)
    c: Horizontal(g7)
    c: Vertical(g6)
    c: Vertical(g8)
    c: PointOnObject(g5,g-1)
    c: Distance(g6) = 1.6
    c: Distance(g0) = 1.6
    c: Coincident(g9,g10)
    c: Coincident(g10,g11)
    c: Coincident(g11,g12)
    c: Coincident(g12,g9)
    c: Horizontal(g9)
    c: Horizontal(g11)
    c: Vertical(g10)
    c: Vertical(g12)
    c: Coincident(g9,g0)
    c: PointOnObject(g10,g5)
    c: Distance(g12) = 2.5
    c: Distance(g1) = 18
    c: Coincident(g13,g14)
    c: Coincident(g14,g15)
    c: Coincident(g15,g16)
    c: Coincident(g16,g13)
    c: Horizontal(g14)
    c: Horizontal(g16)
    c: Vertical(g13)
    c: Vertical(g15)
    c: Symmetric(g14,g13,g17)
    c: PointOnObject(g17,g-2)
    c: PointOnObject(g14,g7)
    c: Distance(g13) = 3.5
    c: Distance(g16) = 9.1
    c: Coincident(g18,g19)
    c: Coincident(g19,g20)
    c: Coincident(g20,g21)
    c: Coincident(g21,g18)
    c: Horizontal(g19)
    c: Horizontal(g21)
    c: Vertical(g18)
    c: Vertical(g20)
    c: Symmetric(g19,g18,g22)
    c: PointOnObject(g22,g-2)
    c: PointOnObject(g19,g1)
    c: Distance(g20,g3) = 3.8
    c: Distance(g21) = 9.5
    c: Coincident(g23,g24)
    c: Coincident(g24,g25)
    c: Coincident(g25,g26)
    c: Coincident(g26,g23)
    c: Horizontal(g24)
    c: Horizontal(g26)
    c: Vertical(g23)
    c: Vertical(g25)
    c: Symmetric(g24,g23,g27)
    c: PointOnObject(g27,g-2)
    c: Distance(g25) = 1.2
    c: Coincident(g28,g29)
    c: Coincident(g29,g30)
    c: Coincident(g30,g31)
    c: Coincident(g31,g28)
    c: Horizontal(g29)
    c: Horizontal(g31)
    c: Vertical(g28)
    c: Vertical(g30)
    c: Symmetric(g29,g28,g32)
    c: Distance(g30) = 13
    c: Distance(g29) = 13
    c: Distance(g30,g7) = 2
    c: Distance(g24,g7) = 2.3
    c: Distance(g32,g-2) = 15.6
    c: Coincident(g33,g34)
    c: Coincident(g34,g35)
    c: Coincident(g35,g36)
    c: Coincident(g36,g33)
    c: Horizontal(g34)
    c: Horizontal(g36)
    c: Vertical(g33)
    c: Vertical(g35)
    c: Symmetric(g34,g33,g37)
    c: Distance(g33) = 1.6
    c: Distance(g33,g5) = 0.6
    c: Coincident(g38,g39)
    c: Coincident(g39,g40)
    c: Coincident(g40,g41)
    c: Coincident(g41,g38)
    c: Horizontal(g39)
    c: Horizontal(g41)
    c: Vertical(g38)
    c: Vertical(g40)
    c: Symmetric(g39,g38,g42)
    c: PointOnObject(g39,g34)
    c: Distance(g40) = 6.4
    c: Coincident(g43,g37)
    c: Coincident(g43,g42)
    c: Vertical(g43)
    c: Coincident(g44,g45)
    c: Coincident(g45,g46)
    c: Coincident(g46,g47)
    c: Coincident(g47,g44)
    c: Horizontal(g45)
    c: Horizontal(g47)
    c: Vertical(g44)
    c: Vertical(g46)
    c: Symmetric(g45,g44,g48)
    c: PointOnObject(g48,g43)
    c: PointOnObject(g45,g5)
    c: Distance(g44) = 5.3
    c: Coincident(g49,g50)
    c: Coincident(g50,g51)
    c: Coincident(g51,g52)
    c: Coincident(g52,g49)
    c: Horizontal(g50)
    c: Horizontal(g52)
    c: Vertical(g49)
    c: Vertical(g51)
    c: Symmetric(g50,g49,g53)
    c: PointOnObject(g53,g43)
    c: Distance(g49,g47) = 4
    c: Diameter(g54) = 25
    c: Distance(g54,g24) = 12.8
    c: Distance(g33,g24) = 4.5
    c: Coincident(g55,g32)
    c: Coincident(g56,g32)
    c: PointOnObject(g56,g29)
    c: Vertical(g56)
    c: PointOnObject(g57,g56)
    c: PointOnObject(g56,g57)
    c: Diameter(g57) = 13
    c: Horizontal(g58)
    c: PointOnObject(g57,g58)
    c: Coincident(g59,g57)
    c: PointOnObject(g59,g58)
    c: PointOnObject(g59,g58)
    c: Radius(g59) = 7
    c: PointOnObject(g60,g59)
    c: PointOnObject(g60,g59)
    c: Horizontal(g60)
    c: Distance(g56,g60) = 2.5
    c: PointOnObject(g61,g29)
    c: PointOnObject(g61,g29)
    c: Coincident(g62,g57)
    c: Coincident(g62,g60)
    c: Coincident(g62,g61)
    c: Coincident(g63,g62)
    c: Coincident(g63,g61)
    c: Coincident(g63,g60)
    c: Coincident(g64,g63)
    c: Coincident(g64,g62)
    c: Coincident(g65,g63)
    c: Horizontal(g65)
    c: Coincident(g66,g65)
    c: PointOnObject(g66,g31)
    c: Vertical(g66)
    c: Coincident(g67,g66)
    c: PointOnObject(g67,g31)
    c: Coincident(g68,g62)
    c: Horizontal(g68)
    c: Coincident(g69,g68)
    c: Coincident(g69,g67)
    c: Vertical(g69)
    c: PointOnObject(g65,g30)
    c: PointOnObject(g68,g28)
FEATURE [Sketcher::SketchObject] Sketch011
  ArcFitTolerance = 0
  AttachmentSupport = -> [XZ_Plane]
  FullyConstrained = false
  MakeInternals = false
  MapMode = 5
  Placement = pos=(0,0,0) rot=(1,0,0;1.5708rad)
  expr: Constraints[105] = Sketch.Constraints[105]
  expr: Constraints[120] = Sketch.Constraints[120]
  expr: Constraints[131] = Sketch.Constraints[131]
  expr: Constraints[132] = Sketch.Constraints[132]
  expr: Constraints[133] = Sketch.Constraints[133]
  expr: Constraints[19] = Sketch.Constraints[19]
  expr: Constraints[20] = Sketch.Constraints[20]
  expr: Constraints[31] = Sketch.Constraints[31]
  expr: Constraints[32] = Sketch.Constraints[32]
  expr: Constraints[44] = Sketch.Constraints[44]
  expr: Constraints[45] = Sketch.Constraints[45]
  expr: Constraints[57] = Sketch.Constraints[57]
  expr: Constraints[58] = Sketch.Constraints[58]
  expr: Constraints[69] = Sketch.Constraints[69]
  expr: Constraints[79] = Sketch.Constraints[79]
  expr: Constraints[80] = Sketch.Constraints[80]
  expr: Constraints[81] = Sketch.Constraints[81]
  expr: Constraints[82] = Sketch.Constraints[82]
  expr: Constraints[83] = Sketch.Constraints[83]
  expr: Constraints[93] = Sketch.Constraints[93]
  expr: Constraints[94] = Sketch.Constraints[94]
  sketch-geometry (73):
    g0: LineSegment [constr] StartX=9 StartY=2.5 StartZ=0 EndX=9 EndY=4.1 EndZ=0
    g1: LineSegment [constr] StartX=9 StartY=4.1 StartZ=0 EndX=-9 EndY=4.1 EndZ=0
    g2: LineSegment [constr] StartX=-9 StartY=4.1 StartZ=0 EndX=-9 EndY=2.5 EndZ=0
    g3: LineSegment [constr] StartX=-9 StartY=2.5 StartZ=0 EndX=9 EndY=2.5 EndZ=0
    g4: GeomPoint [constr] X=0 Y=3.3 Z=0
    g5: LineSegment [constr] StartX=-105.409 StartY=0 StartZ=0 EndX=45.7381 EndY=0 EndZ=0
    g6: LineSegment [constr] StartX=45.7381 StartY=0 StartZ=0 EndX=45.7381 EndY=-1.6 EndZ=0
    g7: LineSegment [constr] StartX=45.7381 StartY=-1.6 StartZ=0 EndX=-105.409 EndY=-1.6 EndZ=0
    g8: LineSegment [constr] StartX=-105.409 StartY=-1.6 StartZ=0 EndX=-105.409 EndY=0 EndZ=0
    g9: LineSegment [constr] StartX=9 StartY=2.5 StartZ=0 EndX=6.36312 EndY=2.5 EndZ=0
    g10: LineSegment [constr] StartX=6.36312 StartY=2.5 StartZ=0 EndX=6.36312 EndY=0 EndZ=0
    g11: LineSegment [constr] StartX=6.36312 StartY=0 StartZ=0 EndX=9 EndY=0 EndZ=0
    g12: LineSegment [constr] StartX=9 StartY=0 StartZ=0 EndX=9 EndY=2.5 EndZ=0
    g13: LineSegment [constr] StartX=4.55 StartY=-5.1 StartZ=0 EndX=4.55 EndY=-1.6 EndZ=0
    g14: LineSegment [constr] StartX=4.55 StartY=-1.6 StartZ=0 EndX=-4.55 EndY=-1.6 EndZ=0
    g15: LineSegment [constr] StartX=-4.55 StartY=-1.6 StartZ=0 EndX=-4.55 EndY=-5.1 EndZ=0
    g16: LineSegment [constr] StartX=-4.55 StartY=-5.1 StartZ=0 EndX=4.55 EndY=-5.1 EndZ=0
    g17: GeomPoint [constr] X=0 Y=-3.35 Z=0
    g18: LineSegment [constr] StartX=-4.75 StartY=6.3 StartZ=0 EndX=-4.75 EndY=4.1 EndZ=0
    g19: LineSegment [constr] StartX=-4.75 StartY=4.1 StartZ=0 EndX=4.75 EndY=4.1 EndZ=0
    g20: LineSegment [constr] StartX=4.75 StartY=4.1 StartZ=0 EndX=4.75 EndY=6.3 EndZ=0
    g21: LineSegment [constr] StartX=4.75 StartY=6.3 StartZ=0 EndX=-4.75 EndY=6.3 EndZ=0
    g22: GeomPoint [constr] X=0 Y=5.2 Z=0
    g23: LineSegment [constr] StartX=-44.4822 StartY=-5.1 StartZ=0 EndX=-44.4822 EndY=-3.9 EndZ=0
    g24: LineSegment [constr] StartX=-44.4822 StartY=-3.9 StartZ=0 EndX=44.4822 EndY=-3.9 EndZ=0
    g25: LineSegment [constr] StartX=44.4822 StartY=-3.9 StartZ=0 EndX=44.4822 EndY=-5.1 EndZ=0
    g26: LineSegment [constr] StartX=44.4822 StartY=-5.1 StartZ=0 EndX=-44.4822 EndY=-5.1 EndZ=0
    g27: GeomPoint [constr] X=0 Y=-4.5 Z=0
    g28: LineSegment [constr] StartX=-9.1 StartY=-3.6 StartZ=0 EndX=-9.1 EndY=9.4 EndZ=0
    g29: LineSegment [constr] StartX=-9.1 StartY=9.4 StartZ=0 EndX=-22.1 EndY=9.4 EndZ=0
    g30: LineSegment [constr] StartX=-22.1 StartY=9.4 StartZ=0 EndX=-22.1 EndY=-3.6 EndZ=0
    g31: LineSegment [constr] StartX=-22.1 StartY=-3.6 StartZ=0 EndX=-9.1 EndY=-3.6 EndZ=0
    g32: GeomPoint [constr] X=-15.6 Y=2.9 Z=0
    g33: LineSegment [constr] StartX=33.0788 StartY=0.6 StartZ=0 EndX=33.0788 EndY=2.2 EndZ=0
    g34: LineSegment [constr] StartX=33.0788 StartY=2.2 StartZ=0 EndX=11.9844 EndY=2.2 EndZ=0
    g35: LineSegment [constr] StartX=11.9844 StartY=2.2 StartZ=0 EndX=11.9844 EndY=0.6 EndZ=0
    g36: LineSegment [constr] StartX=11.9844 StartY=0.6 StartZ=0 EndX=33.0788 EndY=0.6 EndZ=0
    g37: GeomPoint [constr] X=22.5316 Y=1.4 Z=0
    g38: LineSegment [constr] StartX=25.7428 StartY=8.6 StartZ=0 EndX=25.7428 EndY=2.2 EndZ=0
    g39: LineSegment [constr] StartX=25.7428 StartY=2.2 StartZ=0 EndX=19.3204 EndY=2.2 EndZ=0
    g40: LineSegment [constr] StartX=19.3204 StartY=2.2 StartZ=0 EndX=19.3204 EndY=8.6 EndZ=0
    g41: LineSegment [constr] StartX=19.3204 StartY=8.6 StartZ=0 EndX=25.7428 EndY=8.6 EndZ=0
    g42: GeomPoint [constr] X=22.5316 Y=5.4 Z=0
    g43: LineSegment [constr] StartX=22.5316 StartY=1.4 StartZ=0 EndX=22.5316 EndY=5.4 EndZ=0
    g44: LineSegment [constr] StartX=29.8817 StartY=5.3 StartZ=0 EndX=29.8817 EndY=0 EndZ=0
    g45: LineSegment [constr] StartX=29.8817 StartY=0 StartZ=0 EndX=15.1815 EndY=0 EndZ=0
    g46: LineSegment [constr] StartX=15.1815 StartY=0 StartZ=0 EndX=15.1815 EndY=5.3 EndZ=0
    g47: LineSegment [constr] StartX=15.1815 StartY=5.3 StartZ=0 EndX=29.8817 EndY=5.3 EndZ=0
    g48: GeomPoint [constr] X=22.5316 Y=2.65 Z=0
    g49: LineSegment [constr] StartX=28.1684 StartY=6.59315 StartZ=0 EndX=28.1684 EndY=9.3 EndZ=0
    g50: LineSegment [constr] StartX=28.1684 StartY=9.3 StartZ=0 EndX=16.8947 EndY=9.3 EndZ=0
    g51: LineSegment [constr] StartX=16.8947 StartY=9.3 StartZ=0 EndX=16.8947 EndY=6.59315 EndZ=0
    g52: LineSegment [constr] StartX=16.8947 StartY=6.59315 StartZ=0 EndX=28.1684 EndY=6.59315 EndZ=0
    g53: GeomPoint [constr] X=22.5316 Y=7.94657 Z=0
    g54: Circle [constr] CenterX=41.3382 CenterY=8.9 CenterZ=0 NormalX=0 NormalY=0 NormalZ=1 AngleXU=0 Radius=12.5
    g55: LineSegment StartX=2.65 StartY=-2.8 StartZ=0 EndX=2.65 EndY=-5.1 EndZ=0
    g56: LineSegment StartX=2.65 StartY=-5.1 StartZ=0 EndX=-2.65 EndY=-5.1 EndZ=0
    g57: LineSegment StartX=-2.65 StartY=-5.1 StartZ=0 EndX=-2.65 EndY=-2.8 EndZ=0
    g58: LineSegment StartX=-2.65 StartY=-2.8 StartZ=0 EndX=2.65 EndY=-2.8 EndZ=0
    g59: GeomPoint [constr] X=0 Y=-3.95 Z=0
    g60: LineSegment StartX=-4.65 StartY=3.35 StartZ=0 EndX=-4.65 EndY=5.65 EndZ=0
    g61: LineSegment StartX=-4.15 StartY=6.15 StartZ=0 EndX=4.15 EndY=6.15 EndZ=0
    g62: LineSegment StartX=4.65 StartY=5.65 StartZ=0 EndX=4.65 EndY=3.35 EndZ=0
    g63: LineSegment StartX=4.15 StartY=2.85 StartZ=0 EndX=-4.15 EndY=2.85 EndZ=0
    g64: GeomPoint [constr] X=0 Y=4.5 Z=0
    g65: ArcOfCircle CenterX=-4.15 CenterY=5.65 CenterZ=0 NormalX=0 NormalY=0 NormalZ=1 AngleXU=0 Radius=0.5 StartAngle=1.5708 EndAngle=3.14159
    g66: GeomPoint [constr] X=-4.65 Y=6.15 Z=0
    g67: ArcOfCircle CenterX=-4.15 CenterY=3.35 CenterZ=0 NormalX=0 NormalY=0 NormalZ=1 AngleXU=0 Radius=0.5 StartAngle=3.14159 EndAngle=4.71239
    g68: GeomPoint [constr] X=-4.65 Y=2.85 Z=0
    g69: ArcOfCircle CenterX=4.15 CenterY=3.35 CenterZ=0 NormalX=0 NormalY=0 NormalZ=1 AngleXU=0 Radius=0.5 StartAngle=4.71239 EndAngle=6.28319
    g70: GeomPoint [constr] X=4.65 Y=2.85 Z=0
    g71: ArcOfCircle CenterX=4.15 CenterY=5.65 CenterZ=0 NormalX=0 NormalY=0 NormalZ=1 AngleXU=0 Radius=0.5 StartAngle=0 EndAngle=1.5708
    g72: GeomPoint [constr] X=4.65 Y=6.15 Z=0
  constraints (177):
    c: Coincident(g0,g1)
    c: Coincident(g1,g2)
    c: Coincident(g2,g3)
    c: Coincident(g3,g0)
    c: Horizontal(g1)
    c: Horizontal(g3)
    c: Vertical(g0)
    c: Vertical(g2)
    c: Symmetric(g1,g0,g4)
    c: PointOnObject(g4,g-2)
    c: Coincident(g5,g6)
    c: Coincident(g6,g7)
    c: Coincident(g7,g8)
    c: Coincident(g8,g5)
    c: Horizontal(g5)
    c: Horizontal(g7)
    c: Vertical(g6)
    c: Vertical(g8)
    c: PointOnObject(g5,g-1)
    c: Distance(g6) = 1.6
    c: Distance(g0) = 1.6
    c: Coincident(g9,g10)
    c: Coincident(g10,g11)
    c: Coincident(g11,g12)
    c: Coincident(g12,g9)
    c: Horizontal(g9)
    c: Horizontal(g11)
    c: Vertical(g10)
    c: Vertical(g12)
    c: Coincident(g9,g0)
    c: PointOnObject(g10,g5)
    c: Distance(g12) = 2.5
    c: Distance(g1) = 18
    c: Coincident(g13,g14)
    c: Coincident(g14,g15)
    c: Coincident(g15,g16)
    c: Coincident(g16,g13)
    c: Horizontal(g14)
    c: Horizontal(g16)
    c: Vertical(g13)
    c: Vertical(g15)
    c: Symmetric(g14,g13,g17)
    c: PointOnObject(g17,g-2)
    c: PointOnObject(g14,g7)
    c: Distance(g13) = 3.5
    c: Distance(g16) = 9.1
    c: Coincident(g18,g19)
    c: Coincident(g19,g20)
    c: Coincident(g20,g21)
    c: Coincident(g21,g18)
    c: Horizontal(g19)
    c: Horizontal(g21)
    c: Vertical(g18)
    c: Vertical(g20)
    c: Symmetric(g19,g18,g22)
    c: PointOnObject(g22,g-2)
    c: PointOnObject(g19,g1)
    c: Distance(g20,g3) = 3.8
    c: Distance(g21) = 9.5
    c: Coincident(g23,g24)
    c: Coincident(g24,g25)
    c: Coincident(g25,g26)
    c: Coincident(g26,g23)
    c: Horizontal(g24)
    c: Horizontal(g26)
    c: Vertical(g23)
    c: Vertical(g25)
    c: Symmetric(g24,g23,g27)
    c: PointOnObject(g27,g-2)
    c: Distance(g25) = 1.2
    c: Coincident(g28,g29)
    c: Coincident(g29,g30)
    c: Coincident(g30,g31)
    c: Coincident(g31,g28)
    c: Horizontal(g29)
    c: Horizontal(g31)
    c: Vertical(g28)
    c: Vertical(g30)
    c: Symmetric(g29,g28,g32)
    c: Distance(g30) = 13
    c: Distance(g29) = 13
    c: Distance(g30,g7) = 2
    c: Distance(g24,g7) = 2.3
    c: Distance(g32,g-2) = 15.6
    c: Coincident(g33,g34)
    c: Coincident(g34,g35)
    c: Coincident(g35,g36)
    c: Coincident(g36,g33)
    c: Horizontal(g34)
    c: Horizontal(g36)
    c: Vertical(g33)
    c: Vertical(g35)
    c: Symmetric(g34,g33,g37)
    c: Distance(g33) = 1.6
    c: Distance(g33,g5) = 0.6
    c: Coincident(g38,g39)
    c: Coincident(g39,g40)
    c: Coincident(g40,g41)
    c: Coincident(g41,g38)
    c: Horizontal(g39)
    c: Horizontal(g41)
    c: Vertical(g38)
    c: Vertical(g40)
    c: Symmetric(g39,g38,g42)
    c: PointOnObject(g39,g34)
    c: Distance(g40) = 6.4
    c: Coincident(g43,g37)
    c: Coincident(g43,g42)
    c: Vertical(g43)
    c: Coincident(g44,g45)
    c: Coincident(g45,g46)
    c: Coincident(g46,g47)
    c: Coincident(g47,g44)
    c: Horizontal(g45)
    c: Horizontal(g47)
    c: Vertical(g44)
    c: Vertical(g46)
    c: Symmetric(g45,g44,g48)
    c: PointOnObject(g48,g43)
    c: PointOnObject(g45,g5)
    c: Distance(g44) = 5.3
    c: Coincident(g49,g50)
    c: Coincident(g50,g51)
    c: Coincident(g51,g52)
    c: Coincident(g52,g49)
    c: Horizontal(g50)
    c: Horizontal(g52)
    c: Vertical(g49)
    c: Vertical(g51)
    c: Symmetric(g50,g49,g53)
    c: PointOnObject(g53,g43)
    c: Distance(g49,g47) = 4
    c: Diameter(g54) = 25
    c: Distance(g54,g24) = 12.8
    c: Distance(g33,g24) = 4.5
    c: Coincident(g55,g56)
    c: Coincident(g56,g57)
    c: Coincident(g57,g58)
    c: Coincident(g58,g55)
    c: Horizontal(g56)
    c: Horizontal(g58)
    c: Vertical(g55)
    c: Vertical(g57)
    c: Symmetric(g56,g55,g59)
    c: PointOnObject(g59,g-2)
    c: PointOnObject(g56,g16)
    c: Distance(g57) = 2.3
    c: Distance(g56) = 5.3
    c: Horizontal(g61)
    c: Horizontal(g63)
    c: Vertical(g60)
    c: Vertical(g62)
    c: Symmetric(g72,g68,g64)
    c: PointOnObject(g64,g-2)
    c: Distance(g72,g66) = 9.3
    c: Distance(g68,g66) = 3.3
    c: Distance(g68,g3) = 0.35
    c: PointOnObject(g66,g61)
    c: PointOnObject(g66,g60)
    c: Tangent(g61,g65) = 1.5708
    c: Tangent(g60,g65) = 1.5708
    c: PointOnObject(g68,g60)
    c: PointOnObject(g68,g63)
    c: Tangent(g60,g67) = 1.5708
    c: Tangent(g63,g67) = 1.5708
    c: PointOnObject(g70,g63)
    c: PointOnObject(g70,g62)
    c: Tangent(g63,g69) = 1.5708
    c: Tangent(g62,g69) = 1.5708
    c: PointOnObject(g72,g62)
    c: PointOnObject(g72,g61)
    c: Tangent(g62,g71) = 1.5708
    c: Tangent(g61,g71) = 1.5708
    c: Radius(g71) = 0.5
    c: Radius(g69) = 0.5
    c: Radius(g67) = 0.5
    c: Radius(g65) = 0.5
FEATURE [Sketcher::SketchObject] Sketch012
  ArcFitTolerance = 0
  AttachmentSupport = -> [XY_Plane]
  FullyConstrained = true
  MakeInternals = false
  MapMode = 5
  sketch-geometry (7):
    g0: LineSegment StartX=1.1 StartY=-35.4 StartZ=0 EndX=0.55 EndY=-34.4474 EndZ=0
    g1: LineSegment StartX=0.55 StartY=-34.4474 StartZ=0 EndX=-0.55 EndY=-34.4474 EndZ=0
    g2: LineSegment StartX=-0.55 StartY=-34.4474 StartZ=0 EndX=-1.1 EndY=-35.4 EndZ=0
    g3: LineSegment StartX=-1.1 StartY=-35.4 StartZ=0 EndX=-0.55 EndY=-36.3526 EndZ=0
    g4: LineSegment StartX=-0.55 StartY=-36.3526 StartZ=0 EndX=0.55 EndY=-36.3526 EndZ=0
    g5: LineSegment StartX=0.55 StartY=-36.3526 StartZ=0 EndX=1.1 EndY=-35.4 EndZ=0
    g6: Circle [constr] CenterX=0 CenterY=-35.4 CenterZ=0 NormalX=0 NormalY=0 NormalZ=1 AngleXU=0 Radius=1.1
  constraints (17):
    c: Coincident(g0,g1)
    c: Coincident(g1,g2)
    c: Coincident(g2,g3)
    c: Coincident(g3,g4)
    c: Coincident(g4,g5)
    c: Coincident(g5,g0)
    c: Equal(g0, g1-g5) x5
    c: PointOnObject(g0,g6)
    c: PointOnObject(g1,g6)
    c: PointOnObject(g2,g6)
    c: PointOnObject(g3,g6)
    c: PointOnObject(g4,g6)
    c: PointOnObject(g5,g6)
    c: PointOnObject(g6,g-2)
    c: Diameter(g6) = 2.2
    c: Distance(g6,g-1) = 35.4
    c: Horizontal(g4)
FEATURE [Sketcher::SketchObject] Sketch013
  ArcFitTolerance = 0
  AttachmentSupport = -> [XY_Plane]
  FullyConstrained = false
  MakeInternals = false
  MapMode = 5
  sketch-geometry (23):
    g0: ArcOfCircle [constr] CenterX=-17 CenterY=-63.1 CenterZ=0 NormalX=0 NormalY=0 NormalZ=1 AngleXU=0 Radius=1.25 StartAngle=3.14159 EndAngle=6.28319
    g1: ArcOfCircle [constr] CenterX=-17 CenterY=-62.3 CenterZ=0 NormalX=0 NormalY=0 NormalZ=1 AngleXU=0 Radius=1.25 StartAngle=8.7e-15 EndAngle=3.14159
    g2: LineSegment [constr] StartX=-15.75 StartY=-63.1 StartZ=0 EndX=-15.75 EndY=-62.3 EndZ=0
    g3: LineSegment StartX=-18.25 StartY=-62.3 StartZ=0 EndX=-18.25 EndY=-63.1 EndZ=0
    g4: LineSegment [constr] StartX=-17 StartY=-63.1 StartZ=0 EndX=-17 EndY=12.3674 EndZ=0
    g5: ArcOfCircle [constr] CenterX=-17 CenterY=-1.3 CenterZ=0 NormalX=0 NormalY=0 NormalZ=1 AngleXU=0 Radius=1.25 StartAngle=0 EndAngle=3.14159
    g6: ArcOfCircle [constr] CenterX=-17 CenterY=-2.1 CenterZ=0 NormalX=0 NormalY=0 NormalZ=1 AngleXU=0 Radius=1.25 StartAngle=3.14159 EndAngle=6.28319
    g7: LineSegment StartX=-18.25 StartY=-1.3 StartZ=0 EndX=-18.25 EndY=-2.1 EndZ=0
    g8: LineSegment [constr] StartX=-15.75 StartY=-2.1 StartZ=0 EndX=-15.75 EndY=-1.3 EndZ=0
    g9: LineSegment [constr] StartX=-15.75 StartY=-62.3 StartZ=0 EndX=-15.75 EndY=-2.1 EndZ=0
    g10: LineSegment StartX=-18.25 StartY=-2.1 StartZ=0 EndX=-18.25 EndY=-62.3 EndZ=0
    g11: ArcOfCircle CenterX=-17 CenterY=-1.3 CenterZ=0 NormalX=0 NormalY=0 NormalZ=1 AngleXU=0 Radius=1.25 StartAngle=1.5708 EndAngle=3.14159
    g12: ArcOfCircle CenterX=-17 CenterY=-63.1 CenterZ=0 NormalX=0 NormalY=0 NormalZ=1 AngleXU=0 Radius=1.25 StartAngle=3.14159 EndAngle=4.71239
    g13: LineSegment [constr] StartX=-17 StartY=-63.1 StartZ=0 EndX=-17 EndY=-64.35 EndZ=0
    g14: LineSegment StartX=-17 StartY=-0.05 StartZ=0 EndX=-14 EndY=-0.05 EndZ=0
    g15: LineSegment [constr] StartX=-18.25 StartY=-1.3 StartZ=0 EndX=-15.8528 EndY=-1.3 EndZ=0
    g16: LineSegment [constr] StartX=-14 StartY=-0.05 StartZ=0 EndX=-14 EndY=-64.5733 EndZ=0
    g17: LineSegment [constr] StartX=-17 StartY=-64.35 StartZ=0 EndX=-14 EndY=-64.35 EndZ=0
    g18: ArcOfCircle CenterX=-14 CenterY=-1.3 CenterZ=0 NormalX=0 NormalY=0 NormalZ=1 AngleXU=0 Radius=1.25 StartAngle=0 EndAngle=1.5708
    g19: LineSegment StartX=-12.75 StartY=-1.3 StartZ=0 EndX=-12.75 EndY=-63.1 EndZ=0
    g20: LineSegment [constr] StartX=-17 StartY=-63.1 StartZ=0 EndX=-12.75 EndY=-63.1 EndZ=0
    g21: ArcOfCircle CenterX=-14 CenterY=-63.1 CenterZ=0 NormalX=0 NormalY=0 NormalZ=1 AngleXU=0 Radius=1.25 StartAngle=4.71239 EndAngle=6.28319
    g22: LineSegment StartX=-14 StartY=-64.35 StartZ=0 EndX=-17 EndY=-64.35 EndZ=0
  constraints (59):
    c: Tangent(g0,g2) = -1.5708
    c: Tangent(g2,g1) = -1.5708
    c: Tangent(g1,g3) = -1.5708
    c: Tangent(g3,g0) = -1.5708
    c: Equal(g0,g1)
    c: Vertical(g2)
    c: Coincident(g4,g0)
    c: Vertical(g4)
    c: DistanceX(g-2,g0) = -17
    c: Distance(g1,g0) = 0.8
    c: Tangent(g5,g7) = -1.5708
    c: Tangent(g7,g6) = -1.5708
    c: Tangent(g6,g8) = -1.5708
    c: Tangent(g8,g5) = -1.5708
    c: Equal(g5,g6)
    c: PointOnObject(g5,g4)
    c: PointOnObject(g6,g4)
    c: Distance(g5,g8) = 2.5
    c: Distance(g5,g6) = 0.8
    c: Distance(g5,g-1) = 1.3
    c: Distance(g5,g1) = 61
    c: Coincident(g9,g2)
    c: Coincident(g9,g8)
    c: Vertical(g9)
    c: Coincident(g10,g7)
    c: Coincident(g10,g3)
    c: Coincident(g11,g5)
    c: Coincident(g11,g7)
    c: PointOnObject(g11,g4)
    c: Coincident(g12,g0)
    c: Coincident(g12,g3)
    c: Coincident(g13,g12)
    c: Coincident(g13,g12)
    c: Vertical(g13)
    c: Coincident(g14,g11)
    c: Horizontal(g14)
    c: Coincident(g15,g7)
    c: Horizontal(g15)
    c: Coincident(g16,g14)
    c: Vertical(g16)
    c: Coincident(g17,g12)
    c: PointOnObject(g17,g16)
    c: Horizontal(g17)
    c: PointOnObject(g18,g15)
    c: Coincident(g18,g14)
    c: PointOnObject(g18,g15)
    c: PointOnObject(g18,g16)
    c: Coincident(g19,g18)
    c: Vertical(g19)
    c: Coincident(g20,g12)
    c: Coincident(g20,g19)
    c: Horizontal(g20)
    c: PointOnObject(g21,g20)
    c: Coincident(g21,g19)
    c: PointOnObject(g21,g16)
    c: PointOnObject(g21,g16)
    c: Coincident(g22,g21)
    c: Coincident(g22,g12)
    c: Distance(g14) = 3
FEATURE [Sketcher::SketchObject] Sketch014
  ArcFitTolerance = 0
  AttachmentOffset = pos=(0,0,4.5) rot=(0,0,1;0rad)
  AttachmentSupport = -> [XY_Plane]
  FullyConstrained = true
  MakeInternals = false
  MapMode = 5
  Placement = pos=(0,0,4.5) rot=(0,0,1;0rad)
  expr: Constraints[10] = Sketch001.Constraints[10]
  expr: Constraints[12] = Sketch001.Constraints[12]
  expr: Constraints[22] = Sketch001.Constraints[22]
  expr: Constraints[23] = Sketch001.Constraints[23]
  expr: Constraints[24] = Sketch001.Constraints[24]
  expr: Constraints[36] = Sketch001.Constraints[36]
  expr: Constraints[37] = Sketch001.Constraints[37]
  expr: Constraints[48] = Sketch001.Constraints[48]
  expr: Constraints[49] = Sketch001.Constraints[49]
  expr: Constraints[50] = Sketch001.Constraints[50]
  expr: Constraints[51] = Sketch001.Constraints[51]
  sketch-geometry (25):
    g0: LineSegment [constr] StartX=8.4 StartY=-34 StartZ=0 EndX=8.4 EndY=0 EndZ=0
    g1: LineSegment [constr] StartX=8.4 StartY=0 StartZ=0 EndX=-8.4 EndY=0 EndZ=0
    g2: LineSegment [constr] StartX=-8.4 StartY=0 StartZ=0 EndX=-8.4 EndY=-34 EndZ=0
    g3: LineSegment [constr] StartX=-8.4 StartY=-34 StartZ=0 EndX=8.4 EndY=-34 EndZ=0
    g4: GeomPoint [constr] X=0 Y=-17 Z=0
    g5: LineSegment [constr] StartX=-22.1 StartY=-60.7 StartZ=0 EndX=-22.1 EndY=-3.7 EndZ=0
    g6: LineSegment [constr] StartX=-22.1 StartY=-3.7 StartZ=0 EndX=-9.1 EndY=-3.7 EndZ=0
    g7: LineSegment [constr] StartX=-9.1 StartY=-3.7 StartZ=0 EndX=-9.1 EndY=-60.7 EndZ=0
    g8: LineSegment [constr] StartX=-9.1 StartY=-60.7 StartZ=0 EndX=-22.1 EndY=-60.7 EndZ=0
    g9: GeomPoint [constr] X=-15.6 Y=-32.2 Z=0
    g10: LineSegment [constr] StartX=22.1 StartY=-68.9 StartZ=0 EndX=22.1 EndY=0 EndZ=0
    g11: LineSegment [constr] StartX=22.1 StartY=0 StartZ=0 EndX=-22.1 EndY=0 EndZ=0
    g12: LineSegment [constr] StartX=-22.1 StartY=0 StartZ=0 EndX=-22.1 EndY=-68.9 EndZ=0
    g13: LineSegment [constr] StartX=-22.1 StartY=-68.9 StartZ=0 EndX=22.1 EndY=-68.9 EndZ=0
    g14: GeomPoint [constr] X=0 Y=-34.45 Z=0
    g15: LineSegment [constr] StartX=8.5 StartY=-53.9 StartZ=0 EndX=8.5 EndY=-36.9 EndZ=0
    g16: LineSegment [constr] StartX=8.5 StartY=-36.9 StartZ=0 EndX=-8.5 EndY=-36.9 EndZ=0
    g17: LineSegment [constr] StartX=-8.5 StartY=-36.9 StartZ=0 EndX=-8.5 EndY=-53.9 EndZ=0
    g18: LineSegment [constr] StartX=-8.5 StartY=-53.9 StartZ=0 EndX=8.5 EndY=-53.9 EndZ=0
    g19: GeomPoint [constr] X=0 Y=-45.4 Z=0
    g20: LineSegment StartX=-8.5 StartY=-36.6 StartZ=0 EndX=-8.5 EndY=-34.5 EndZ=0
    g21: LineSegment StartX=-8.5 StartY=-34.5 StartZ=0 EndX=8.5 EndY=-34.5 EndZ=0
    g22: LineSegment StartX=8.5 StartY=-34.5 StartZ=0 EndX=8.5 EndY=-36.6 EndZ=0
    g23: LineSegment StartX=8.5 StartY=-36.6 StartZ=0 EndX=-8.5 EndY=-36.6 EndZ=0
    g24: GeomPoint [constr] X=0 Y=-35.55 Z=0
  constraints (65):
    c: Coincident(g0,g1)
    c: Coincident(g1,g2)
    c: Coincident(g2,g3)
    c: Coincident(g3,g0)
    c: Horizontal(g1)
    c: Horizontal(g3)
    c: Vertical(g0)
    c: Vertical(g2)
    c: Symmetric(g1,g0,g4)
    c: PointOnObject(g4,g-2)
    c: Distance(g0) = 34
    c: PointOnObject(g-1,g1)
    c: Distance(g3) = 16.8
    c: Coincident(g5,g6)
    c: Coincident(g6,g7)
    c: Coincident(g7,g8)
    c: Coincident(g8,g5)
    c: Horizontal(g6)
    c: Horizontal(g8)
    c: Vertical(g5)
    c: Vertical(g7)
    c: Symmetric(g6,g5,g9)
    c: Distance(g6) = 13
    c: Distance(g5) = 57
    c: Distance(g9,g-1) = 32.2
    c: Coincident(g10,g11)
    c: Coincident(g11,g12)
    c: Coincident(g12,g13)
    c: Coincident(g13,g10)
    c: Horizontal(g11)
    c: Horizontal(g13)
    c: Vertical(g10)
    c: Vertical(g12)
    c: Symmetric(g11,g10,g14)
    c: PointOnObject(g14,g-2)
    c: PointOnObject(g11,g-1)
    c: Distance(g12,g-2) = 22.1
    c: Distance(g10) = 68.9
    c: Coincident(g15,g16)
    c: Coincident(g16,g17)
    c: Coincident(g17,g18)
    c: Coincident(g18,g15)
    c: Horizontal(g16)
    c: Horizontal(g18)
    c: Vertical(g15)
    c: Vertical(g17)
    c: Symmetric(g16,g15,g19)
    c: PointOnObject(g19,g-2)
    c: Distance(g18) = 17
    c: Distance(g15) = 17
    c: Distance(g19,g-1) = 45.4
    c: Distance(g9,g-2) = 15.6
    c: Coincident(g20,g21)
    c: Coincident(g21,g22)
    c: Coincident(g22,g23)
    c: Coincident(g23,g20)
    c: Horizontal(g21)
    c: Horizontal(g23)
    c: Vertical(g20)
    c: Vertical(g22)
    c: Symmetric(g21,g20,g24)
    c: PointOnObject(g24,g-2)
    c: Distance(g22) = 2.1
    c: Distance(g21) = 17
    c: Distance(g16,g23) = 0.3
FEATURE [Sketcher::SketchObject] Sketch016
  ArcFitTolerance = 0
  AttachmentSupport = -> [XZ_Plane]
  FullyConstrained = false
  MakeInternals = false
  MapMode = 5
  Placement = pos=(0,0,0) rot=(1,0,0;1.5708rad)
  expr: Constraints[105] = Sketch.Constraints[105]
  expr: Constraints[120] = Sketch.Constraints[120]
  expr: Constraints[131] = Sketch.Constraints[131]
  expr: Constraints[132] = Sketch.Constraints[132]
  expr: Constraints[133] = Sketch.Constraints[133]
  expr: Constraints[19] = Sketch.Constraints[19]
  expr: Constraints[20] = Sketch.Constraints[20]
  expr: Constraints[31] = Sketch.Constraints[31]
  expr: Constraints[32] = Sketch.Constraints[32]
  expr: Constraints[44] = Sketch.Constraints[44]
  expr: Constraints[45] = Sketch.Constraints[45]
  expr: Constraints[57] = Sketch.Constraints[57]
  expr: Constraints[58] = Sketch.Constraints[58]
  expr: Constraints[69] = Sketch.Constraints[69]
  expr: Constraints[79] = Sketch.Constraints[79]
  expr: Constraints[80] = Sketch.Constraints[80]
  expr: Constraints[81] = Sketch.Constraints[81]
  expr: Constraints[82] = Sketch.Constraints[82]
  expr: Constraints[83] = Sketch.Constraints[83]
  expr: Constraints[93] = Sketch.Constraints[93]
  expr: Constraints[94] = Sketch.Constraints[94]
  sketch-geometry (62):
    g0: LineSegment [constr] StartX=9 StartY=2.5 StartZ=0 EndX=9 EndY=4.1 EndZ=0
    g1: LineSegment [constr] StartX=9 StartY=4.1 StartZ=0 EndX=-9 EndY=4.1 EndZ=0
    g2: LineSegment [constr] StartX=-9 StartY=4.1 StartZ=0 EndX=-9 EndY=2.5 EndZ=0
    g3: LineSegment [constr] StartX=-9 StartY=2.5 StartZ=0 EndX=9 EndY=2.5 EndZ=0
    g4: GeomPoint [constr] X=0 Y=3.3 Z=0
    g5: LineSegment [constr] StartX=-105.409 StartY=0 StartZ=0 EndX=45.7381 EndY=0 EndZ=0
    g6: LineSegment [constr] StartX=45.7381 StartY=0 StartZ=0 EndX=45.7381 EndY=-1.6 EndZ=0
    g7: LineSegment [constr] StartX=45.7381 StartY=-1.6 StartZ=0 EndX=-105.409 EndY=-1.6 EndZ=0
    g8: LineSegment [constr] StartX=-105.409 StartY=-1.6 StartZ=0 EndX=-105.409 EndY=0 EndZ=0
    g9: LineSegment [constr] StartX=9 StartY=2.5 StartZ=0 EndX=6.36312 EndY=2.5 EndZ=0
    g10: LineSegment [constr] StartX=6.36312 StartY=2.5 StartZ=0 EndX=6.36312 EndY=0 EndZ=0
    g11: LineSegment [constr] StartX=6.36312 StartY=0 StartZ=0 EndX=9 EndY=0 EndZ=0
    g12: LineSegment [constr] StartX=9 StartY=0 StartZ=0 EndX=9 EndY=2.5 EndZ=0
    g13: LineSegment [constr] StartX=4.55 StartY=-5.1 StartZ=0 EndX=4.55 EndY=-1.6 EndZ=0
    g14: LineSegment [constr] StartX=4.55 StartY=-1.6 StartZ=0 EndX=-4.55 EndY=-1.6 EndZ=0
    g15: LineSegment [constr] StartX=-4.55 StartY=-1.6 StartZ=0 EndX=-4.55 EndY=-5.1 EndZ=0
    g16: LineSegment [constr] StartX=-4.55 StartY=-5.1 StartZ=0 EndX=4.55 EndY=-5.1 EndZ=0
    g17: GeomPoint [constr] X=0 Y=-3.35 Z=0
    g18: LineSegment [constr] StartX=-4.75 StartY=6.3 StartZ=0 EndX=-4.75 EndY=4.1 EndZ=0
    g19: LineSegment [constr] StartX=-4.75 StartY=4.1 StartZ=0 EndX=4.75 EndY=4.1 EndZ=0
    g20: LineSegment [constr] StartX=4.75 StartY=4.1 StartZ=0 EndX=4.75 EndY=6.3 EndZ=0
    g21: LineSegment [constr] StartX=4.75 StartY=6.3 StartZ=0 EndX=-4.75 EndY=6.3 EndZ=0
    g22: GeomPoint [constr] X=0 Y=5.2 Z=0
    g23: LineSegment [constr] StartX=-44.4822 StartY=-5.1 StartZ=0 EndX=-44.4822 EndY=-3.9 EndZ=0
    g24: LineSegment [constr] StartX=-44.4822 StartY=-3.9 StartZ=0 EndX=44.4822 EndY=-3.9 EndZ=0
    g25: LineSegment [constr] StartX=44.4822 StartY=-3.9 StartZ=0 EndX=44.4822 EndY=-5.1 EndZ=0
    g26: LineSegment [constr] StartX=44.4822 StartY=-5.1 StartZ=0 EndX=-44.4822 EndY=-5.1 EndZ=0
    g27: GeomPoint [constr] X=0 Y=-4.5 Z=0
    g28: LineSegment [constr] StartX=-9.1 StartY=-3.6 StartZ=0 EndX=-9.1 EndY=9.4 EndZ=0
    g29: LineSegment [constr] StartX=-9.1 StartY=9.4 StartZ=0 EndX=-22.1 EndY=9.4 EndZ=0
    g30: LineSegment [constr] StartX=-22.1 StartY=9.4 StartZ=0 EndX=-22.1 EndY=-3.6 EndZ=0
    g31: LineSegment [constr] StartX=-22.1 StartY=-3.6 StartZ=0 EndX=-9.1 EndY=-3.6 EndZ=0
    g32: GeomPoint [constr] X=-15.6 Y=2.9 Z=0
    g33: LineSegment [constr] StartX=33.0788 StartY=0.6 StartZ=0 EndX=33.0788 EndY=2.2 EndZ=0
    g34: LineSegment [constr] StartX=33.0788 StartY=2.2 StartZ=0 EndX=11.9844 EndY=2.2 EndZ=0
    g35: LineSegment [constr] StartX=11.9844 StartY=2.2 StartZ=0 EndX=11.9844 EndY=0.6 EndZ=0
    g36: LineSegment [constr] StartX=11.9844 StartY=0.6 StartZ=0 EndX=33.0788 EndY=0.6 EndZ=0
    g37: GeomPoint [constr] X=22.5316 Y=1.4 Z=0
    g38: LineSegment [constr] StartX=25.7428 StartY=8.6 StartZ=0 EndX=25.7428 EndY=2.2 EndZ=0
    g39: LineSegment [constr] StartX=25.7428 StartY=2.2 StartZ=0 EndX=19.3204 EndY=2.2 EndZ=0
    g40: LineSegment [constr] StartX=19.3204 StartY=2.2 StartZ=0 EndX=19.3204 EndY=8.6 EndZ=0
    g41: LineSegment [constr] StartX=19.3204 StartY=8.6 StartZ=0 EndX=25.7428 EndY=8.6 EndZ=0
    g42: GeomPoint [constr] X=22.5316 Y=5.4 Z=0
    g43: LineSegment [constr] StartX=22.5316 StartY=1.4 StartZ=0 EndX=22.5316 EndY=5.4 EndZ=0
    g44: LineSegment [constr] StartX=29.8817 StartY=5.3 StartZ=0 EndX=29.8817 EndY=0 EndZ=0
    g45: LineSegment [constr] StartX=29.8817 StartY=0 StartZ=0 EndX=15.1815 EndY=0 EndZ=0
    g46: LineSegment [constr] StartX=15.1815 StartY=0 StartZ=0 EndX=15.1815 EndY=5.3 EndZ=0
    g47: LineSegment [constr] StartX=15.1815 StartY=5.3 StartZ=0 EndX=29.8817 EndY=5.3 EndZ=0
    g48: GeomPoint [constr] X=22.5316 Y=2.65 Z=0
    g49: LineSegment [constr] StartX=28.1684 StartY=6.59315 StartZ=0 EndX=28.1684 EndY=9.3 EndZ=0
    g50: LineSegment [constr] StartX=28.1684 StartY=9.3 StartZ=0 EndX=16.8947 EndY=9.3 EndZ=0
    g51: LineSegment [constr] StartX=16.8947 StartY=9.3 StartZ=0 EndX=16.8947 EndY=6.59315 EndZ=0
    g52: LineSegment [constr] StartX=16.8947 StartY=6.59315 StartZ=0 EndX=28.1684 EndY=6.59315 EndZ=0
    g53: GeomPoint [constr] X=22.5316 Y=7.94657 Z=0
    g54: Circle [constr] CenterX=41.3382 CenterY=8.9 CenterZ=0 NormalX=0 NormalY=0 NormalZ=1 AngleXU=0 Radius=12.5
    g55: LineSegment [constr] StartX=-18.7 StartY=4.8 StartZ=0 EndX=-18.7 EndY=10.6 EndZ=0
    g56: LineSegment [constr] StartX=-18.7 StartY=4.8 StartZ=0 EndX=-30.5234 EndY=4.8 EndZ=0
    g57: ArcOfCircle CenterX=-18.7 CenterY=4.8 CenterZ=0 NormalX=0 NormalY=0 NormalZ=1 AngleXU=0 Radius=5.8 StartAngle=1.5708 EndAngle=3.14159
    g58: LineSegment StartX=-24.5 StartY=4.8 StartZ=0 EndX=-32.4732 EndY=4.8 EndZ=0
    g59: LineSegment StartX=-32.4732 StartY=4.8 StartZ=0 EndX=-32.4732 EndY=15.4079 EndZ=0
    g60: LineSegment StartX=-32.4732 StartY=15.4079 StartZ=0 EndX=-18.7 EndY=15.4079 EndZ=0
    g61: LineSegment StartX=-18.7 StartY=15.4079 StartZ=0 EndX=-18.7 EndY=10.6 EndZ=0
  constraints (153):
    c: Coincident(g0,g1)
    c: Coincident(g1,g2)
    c: Coincident(g2,g3)
    c: Coincident(g3,g0)
    c: Horizontal(g1)
    c: Horizontal(g3)
    c: Vertical(g0)
    c: Vertical(g2)
    c: Symmetric(g1,g0,g4)
    c: PointOnObject(g4,g-2)
    c: Coincident(g5,g6)
    c: Coincident(g6,g7)
    c: Coincident(g7,g8)
    c: Coincident(g8,g5)
    c: Horizontal(g5)
    c: Horizontal(g7)
    c: Vertical(g6)
    c: Vertical(g8)
    c: PointOnObject(g5,g-1)
    c: Distance(g6) = 1.6
    c: Distance(g0) = 1.6
    c: Coincident(g9,g10)
    c: Coincident(g10,g11)
    c: Coincident(g11,g12)
    c: Coincident(g12,g9)
    c: Horizontal(g9)
    c: Horizontal(g11)
    c: Vertical(g10)
    c: Vertical(g12)
    c: Coincident(g9,g0)
    c: PointOnObject(g10,g5)
    c: Distance(g12) = 2.5
    c: Distance(g1) = 18
    c: Coincident(g13,g14)
    c: Coincident(g14,g15)
    c: Coincident(g15,g16)
    c: Coincident(g16,g13)
    c: Horizontal(g14)
    c: Horizontal(g16)
    c: Vertical(g13)
    c: Vertical(g15)
    c: Symmetric(g14,g13,g17)
    c: PointOnObject(g17,g-2)
    c: PointOnObject(g14,g7)
    c: Distance(g13) = 3.5
    c: Distance(g16) = 9.1
    c: Coincident(g18,g19)
    c: Coincident(g19,g20)
    c: Coincident(g20,g21)
    c: Coincident(g21,g18)
    c: Horizontal(g19)
    c: Horizontal(g21)
    c: Vertical(g18)
    c: Vertical(g20)
    c: Symmetric(g19,g18,g22)
    c: PointOnObject(g22,g-2)
    c: PointOnObject(g19,g1)
    c: Distance(g20,g3) = 3.8
    c: Distance(g21) = 9.5
    c: Coincident(g23,g24)
    c: Coincident(g24,g25)
    c: Coincident(g25,g26)
    c: Coincident(g26,g23)
    c: Horizontal(g24)
    c: Horizontal(g26)
    c: Vertical(g23)
    c: Vertical(g25)
    c: Symmetric(g24,g23,g27)
    c: PointOnObject(g27,g-2)
    c: Distance(g25) = 1.2
    c: Coincident(g28,g29)
    c: Coincident(g29,g30)
    c: Coincident(g30,g31)
    c: Coincident(g31,g28)
    c: Horizontal(g29)
    c: Horizontal(g31)
    c: Vertical(g28)
    c: Vertical(g30)
    c: Symmetric(g29,g28,g32)
    c: Distance(g30) = 13
    c: Distance(g29) = 13
    c: Distance(g30,g7) = 2
    c: Distance(g24,g7) = 2.3
    c: Distance(g32,g-2) = 15.6
    c: Coincident(g33,g34)
    c: Coincident(g34,g35)
    c: Coincident(g35,g36)
    c: Coincident(g36,g33)
    c: Horizontal(g34)
    c: Horizontal(g36)
    c: Vertical(g33)
    c: Vertical(g35)
    c: Symmetric(g34,g33,g37)
    c: Distance(g33) = 1.6
    c: Distance(g33,g5) = 0.6
    c: Coincident(g38,g39)
    c: Coincident(g39,g40)
    c: Coincident(g40,g41)
    c: Coincident(g41,g38)
    c: Horizontal(g39)
    c: Horizontal(g41)
    c: Vertical(g38)
    c: Vertical(g40)
    c: Symmetric(g39,g38,g42)
    c: PointOnObject(g39,g34)
    c: Distance(g40) = 6.4
    c: Coincident(g43,g37)
    c: Coincident(g43,g42)
    c: Vertical(g43)
    c: Coincident(g44,g45)
    c: Coincident(g45,g46)
    c: Coincident(g46,g47)
    c: Coincident(g47,g44)
    c: Horizontal(g45)
    c: Horizontal(g47)
    c: Vertical(g44)
    c: Vertical(g46)
    c: Symmetric(g45,g44,g48)
    c: PointOnObject(g48,g43)
    c: PointOnObject(g45,g5)
    c: Distance(g44) = 5.3
    c: Coincident(g49,g50)
    c: Coincident(g50,g51)
    c: Coincident(g51,g52)
    c: Coincident(g52,g49)
    c: Horizontal(g50)
    c: Horizontal(g52)
    c: Vertical(g49)
    c: Vertical(g51)
    c: Symmetric(g50,g49,g53)
    c: PointOnObject(g53,g43)
    c: Distance(g49,g47) = 4
    c: Diameter(g54) = 25
    c: Distance(g54,g24) = 12.8
    c: Distance(g33,g24) = 4.5
    c: Vertical(g55)
    c: Coincident(g56,g55)
    c: Horizontal(g56)
    c: Coincident(g57,g55)
    c: Coincident(g57,g55)
    c: PointOnObject(g57,g56)
    c: Distance(g57,g29) = 1.2
    c: Coincident(g58,g57)
    c: Horizontal(g58)
    c: Coincident(g59,g58)
    c: Vertical(g59)
    c: Coincident(g60,g59)
    c: Horizontal(g60)
    c: Coincident(g61,g60)
    c: Coincident(g61,g57)
    c: Vertical(g61)
    c: DistanceX(g57,g-1) = 24.5
    c: Radius(g57) = 5.8
FEATURE [Sketcher::SketchObject] Sketch017
  ArcFitTolerance = 0
  AttachmentOffset = pos=(0,0,-1.6) rot=(0,0,1;0rad)
  AttachmentSupport = -> [XY_Plane]
  FullyConstrained = false
  MakeInternals = false
  MapMode = 5
  Placement = pos=(0,0,-1.6) rot=(0,0,1;0rad)
  expr: .AttachmentOffset.Base.z = -1.6
  expr: Constraints[10] = Sketch001.Constraints[10]
  expr: Constraints[12] = Sketch001.Constraints[12]
  expr: Constraints[22] = Sketch001.Constraints[22]
  expr: Constraints[23] = Sketch001.Constraints[23]
  expr: Constraints[24] = Sketch001.Constraints[24]
  expr: Constraints[31] = Sketch001.Constraints[37]
  expr: Constraints[42] = Sketch001.Constraints[48]
  expr: Constraints[43] = Sketch001.Constraints[49]
  expr: Constraints[44] = Sketch001.Constraints[50]
  expr: Constraints[45] = Sketch001.Constraints[51]
  sketch-geometry (30):
    g0: LineSegment [constr] StartX=8.4 StartY=-34 StartZ=0 EndX=8.4 EndY=0 EndZ=0
    g1: LineSegment [constr] StartX=8.4 StartY=0 StartZ=0 EndX=-8.4 EndY=0 EndZ=0
    g2: LineSegment [constr] StartX=-8.4 StartY=0 StartZ=0 EndX=-8.4 EndY=-34 EndZ=0
    g3: LineSegment [constr] StartX=-8.4 StartY=-34 StartZ=0 EndX=8.4 EndY=-34 EndZ=0
    g4: GeomPoint [constr] X=0 Y=-17 Z=0
    g5: LineSegment [constr] StartX=-22.1 StartY=-60.7 StartZ=0 EndX=-22.1 EndY=-3.7 EndZ=0
    g6: LineSegment [constr] StartX=-22.1 StartY=-3.7 StartZ=0 EndX=-9.1 EndY=-3.7 EndZ=0
    g7: LineSegment [constr] StartX=-9.1 StartY=-3.7 StartZ=0 EndX=-9.1 EndY=-60.7 EndZ=0
    g8: LineSegment [constr] StartX=-9.1 StartY=-60.7 StartZ=0 EndX=-22.1 EndY=-60.7 EndZ=0
    g9: GeomPoint [constr] X=-15.6 Y=-32.2 Z=0
    g10: LineSegment [constr] StartX=21.5 StartY=-68.9 StartZ=0 EndX=21.5 EndY=0 EndZ=0
    g11: LineSegment [constr] StartX=21.5 StartY=0 StartZ=0 EndX=-21.5 EndY=0 EndZ=0
    g12: GeomPoint [constr] X=0 Y=-34.45 Z=0
    g13: LineSegment [constr] StartX=8.5 StartY=-53.9 StartZ=0 EndX=8.5 EndY=-36.9 EndZ=0
    g14: LineSegment [constr] StartX=8.5 StartY=-36.9 StartZ=0 EndX=-8.5 EndY=-36.9 EndZ=0
    g15: LineSegment [constr] StartX=-8.5 StartY=-36.9 StartZ=0 EndX=-8.5 EndY=-53.9 EndZ=0
    g16: LineSegment [constr] StartX=-8.5 StartY=-53.9 StartZ=0 EndX=8.5 EndY=-53.9 EndZ=0
    g17: GeomPoint [constr] X=0 Y=-45.4 Z=0
    g18: LineSegment StartX=-18.1 StartY=-59.7 StartZ=0 EndX=-24.1 EndY=-59.7 EndZ=0
    g19: LineSegment [constr] StartX=-24.1 StartY=-59.7 StartZ=0 EndX=-24.1 EndY=-64.7 EndZ=0
    g20: LineSegment [constr] StartX=-24.1 StartY=-64.7 StartZ=0 EndX=-18.1 EndY=-64.7 EndZ=0
    g21: LineSegment StartX=-18.1 StartY=-64.7 StartZ=0 EndX=-18.1 EndY=-59.7 EndZ=0
    g22: LineSegment [constr] StartX=-24.1 StartY=-3.3 StartZ=0 EndX=-24.1 EndY=-59.7 EndZ=0
    g23: LineSegment [constr] StartX=-18.1 StartY=-3.3 StartZ=0 EndX=-18.1 EndY=-59.7 EndZ=0
    g24: LineSegment StartX=-24.1 StartY=-59.7 StartZ=0 EndX=-22.2801 EndY=-64.7 EndZ=0
    g25: LineSegment StartX=-18.1 StartY=-64.7 StartZ=0 EndX=-22.2801 EndY=-64.7 EndZ=0
    g26: LineSegment StartX=5 StartY=0 StartZ=0 EndX=5 EndY=-1.2 EndZ=0
    g27: LineSegment StartX=5 StartY=-1.2 StartZ=0 EndX=9 EndY=-1.2 EndZ=0
    g28: LineSegment StartX=9 StartY=-1.2 StartZ=0 EndX=9 EndY=0 EndZ=0
    g29: LineSegment StartX=9 StartY=0 StartZ=0 EndX=5 EndY=0 EndZ=0
  constraints (79):
    c: Coincident(g0,g1)
    c: Coincident(g1,g2)
    c: Coincident(g2,g3)
    c: Coincident(g3,g0)
    c: Horizontal(g1)
    c: Horizontal(g3)
    c: Vertical(g0)
    c: Vertical(g2)
    c: Symmetric(g1,g0,g4)
    c: PointOnObject(g4,g-2)
    c: Distance(g0) = 34
    c: PointOnObject(g-1,g1)
    c: Distance(g3) = 16.8
    c: Coincident(g5,g6)
    c: Coincident(g6,g7)
    c: Coincident(g7,g8)
    c: Coincident(g8,g5)
    c: Horizontal(g6)
    c: Horizontal(g8)
    c: Vertical(g5)
    c: Vertical(g7)
    c: Symmetric(g6,g5,g9)
    c: Distance(g6) = 13
    c: Distance(g5) = 57
    c: Distance(g9,g-1) = 32.2
    c: Coincident(g10,g11)
    c: Horizontal(g11)
    c: Vertical(g10)
    c: Symmetric(g11,g10,g12)
    c: PointOnObject(g12,g-2)
    c: PointOnObject(g11,g-1)
    c: Distance(g10) = 68.9
    c: Coincident(g13,g14)
    c: Coincident(g14,g15)
    c: Coincident(g15,g16)
    c: Coincident(g16,g13)
    c: Horizontal(g14)
    c: Horizontal(g16)
    c: Vertical(g13)
    c: Vertical(g15)
    c: Symmetric(g14,g13,g17)
    c: PointOnObject(g17,g-2)
    c: Distance(g16) = 17
    c: Distance(g13) = 17
    c: Distance(g17,g-1) = 45.4
    c: Distance(g9,g-2) = 15.6
    c: Coincident(g18,g19)
    c: Coincident(g19,g20)
    c: Coincident(g20,g21)
    c: Coincident(g21,g18)
    c: Horizontal(g18)
    c: Horizontal(g20)
    c: Vertical(g19)
    c: Vertical(g21)
    c: Distance(g18,g8) = 1
    c: Distance(g19) = 5
    c: Distance(g20) = 6
    c: Distance(g20,g-2) = 18.1
    c: Coincident(g22,g18)
    c: Vertical(g22)
    c: Coincident(g23,g18)
    c: Vertical(g23)
    c: Coincident(g24,g18)
    c: PointOnObject(g24,g20)
    c: Coincident(g25,g20)
    c: Coincident(g25,g24)
    c: Coincident(g26,g27)
    c: Coincident(g27,g28)
    c: Coincident(g28,g29)
    c: Coincident(g29,g26)
    c: Vertical(g26)
    c: Vertical(g28)
    c: Horizontal(g27)
    c: Horizontal(g29)
    c: PointOnObject(g26,g1)
    c: DistanceX(g27,g27) = 4
    c: DistanceY(g28,g28) = 1.2
    c: DistanceX(g-1,g26) = 5
    c: Angle(g25,g24) = 1.91986
FEATURE [Sketcher::SketchObject] Sketch018
  ArcFitTolerance = 1e-06
  AttachmentSupport = -> [XY_Plane]
  FullyConstrained = false
  MakeInternals = false
  MapMode = 5
  expr: Constraints[10] = Sketch001.Constraints[10]
  expr: Constraints[12] = Sketch001.Constraints[12]
  expr: Constraints[22] = Sketch001.Constraints[22]
  expr: Constraints[23] = Sketch001.Constraints[23]
  expr: Constraints[24] = Sketch001.Constraints[24]
  expr: Constraints[36] = Sketch001.Constraints[36]
  expr: Constraints[37] = Sketch001.Constraints[37]
  expr: Constraints[48] = Sketch001.Constraints[48]
  expr: Constraints[49] = Sketch001.Constraints[49]
  expr: Constraints[50] = Sketch001.Constraints[50]
  expr: Constraints[51] = Sketch001.Constraints[51]
  sketch-geometry (24):
    g0: LineSegment [constr] StartX=8.4 StartY=-34 StartZ=0 EndX=8.4 EndY=0 EndZ=0
    g1: LineSegment [constr] StartX=8.4 StartY=0 StartZ=0 EndX=-8.4 EndY=0 EndZ=0
    g2: LineSegment [constr] StartX=-8.4 StartY=0 StartZ=0 EndX=-8.4 EndY=-34 EndZ=0
    g3: LineSegment [constr] StartX=-8.4 StartY=-34 StartZ=0 EndX=8.4 EndY=-34 EndZ=0
    g4: GeomPoint [constr] X=0 Y=-17 Z=0
    g5: LineSegment [constr] StartX=-22.1 StartY=-60.7 StartZ=0 EndX=-22.1 EndY=-3.7 EndZ=0
    g6: LineSegment [constr] StartX=-22.1 StartY=-3.7 StartZ=0 EndX=-9.1 EndY=-3.7 EndZ=0
    g7: LineSegment [constr] StartX=-9.1 StartY=-3.7 StartZ=0 EndX=-9.1 EndY=-60.7 EndZ=0
    g8: LineSegment [constr] StartX=-9.1 StartY=-60.7 StartZ=0 EndX=-22.1 EndY=-60.7 EndZ=0
    g9: GeomPoint [constr] X=-15.6 Y=-32.2 Z=0
    g10: LineSegment [constr] StartX=22.1 StartY=-68.9 StartZ=0 EndX=22.1 EndY=0 EndZ=0
    g11: LineSegment [constr] StartX=22.1 StartY=0 StartZ=0 EndX=-22.1 EndY=0 EndZ=0
    g12: LineSegment [constr] StartX=-22.1 StartY=0 StartZ=0 EndX=-22.1 EndY=-68.9 EndZ=0
    g13: LineSegment [constr] StartX=-22.1 StartY=-68.9 StartZ=0 EndX=22.1 EndY=-68.9 EndZ=0
    g14: GeomPoint [constr] X=0 Y=-34.45 Z=0
    g15: LineSegment [constr] StartX=8.5 StartY=-53.9 StartZ=0 EndX=8.5 EndY=-36.9 EndZ=0
    g16: LineSegment [constr] StartX=8.5 StartY=-36.9 StartZ=0 EndX=-8.5 EndY=-36.9 EndZ=0
    g17: LineSegment [constr] StartX=-8.5 StartY=-36.9 StartZ=0 EndX=-8.5 EndY=-53.9 EndZ=0
    g18: LineSegment [constr] StartX=-8.5 StartY=-53.9 StartZ=0 EndX=8.5 EndY=-53.9 EndZ=0
    g19: GeomPoint [constr] X=0 Y=-45.4 Z=0
    g20: LineSegment StartX=-8.7 StartY=0 StartZ=0 EndX=-8.7 EndY=-40.9123 EndZ=0
    g21: LineSegment StartX=-8.7 StartY=-40.9123 StartZ=0 EndX=22.1 EndY=-40.9123 EndZ=0
    g22: LineSegment StartX=22.1 StartY=-40.9123 StartZ=0 EndX=22.1 EndY=0 EndZ=0
    g23: LineSegment StartX=22.1 StartY=0 StartZ=0 EndX=-8.7 EndY=0 EndZ=0
  constraints (63):
    c: Coincident(g0,g1)
    c: Coincident(g1,g2)
    c: Coincident(g2,g3)
    c: Coincident(g3,g0)
    c: Horizontal(g1)
    c: Horizontal(g3)
    c: Vertical(g0)
    c: Vertical(g2)
    c: Symmetric(g1,g0,g4)
    c: PointOnObject(g4,g-2)
    c: Distance(g0) = 34
    c: PointOnObject(g-1,g1)
    c: Distance(g3) = 16.8
    c: Coincident(g5,g6)
    c: Coincident(g6,g7)
    c: Coincident(g7,g8)
    c: Coincident(g8,g5)
    c: Horizontal(g6)
    c: Horizontal(g8)
    c: Vertical(g5)
    c: Vertical(g7)
    c: Symmetric(g6,g5,g9)
    c: Distance(g6) = 13
    c: Distance(g5) = 57
    c: Distance(g9,g-1) = 32.2
    c: Coincident(g10,g11)
    c: Coincident(g11,g12)
    c: Coincident(g12,g13)
    c: Coincident(g13,g10)
    c: Horizontal(g11)
    c: Horizontal(g13)
    c: Vertical(g10)
    c: Vertical(g12)
    c: Symmetric(g11,g10,g14)
    c: PointOnObject(g14,g-2)
    c: PointOnObject(g11,g-1)
    c: Distance(g12,g-2) = 22.1
    c: Distance(g10) = 68.9
    c: Coincident(g15,g16)
    c: Coincident(g16,g17)
    c: Coincident(g17,g18)
    c: Coincident(g18,g15)
    c: Horizontal(g16)
    c: Horizontal(g18)
    c: Vertical(g15)
    c: Vertical(g17)
    c: Symmetric(g16,g15,g19)
    c: PointOnObject(g19,g-2)
    c: Distance(g18) = 17
    c: Distance(g15) = 17
    c: Distance(g19,g-1) = 45.4
    c: Distance(g9,g-2) = 15.6
    c: Coincident(g20,g21)
    c: Coincident(g21,g22)
    c: Coincident(g22,g23)
    c: Coincident(g23,g20)
    c: Vertical(g20)
    c: Vertical(g22)
    c: Horizontal(g21)
    c: Horizontal(g23)
    c: PointOnObject(g20,g11)
    c: PointOnObject(g21,g10)
    c: Distance(g2,g20) = 0.3
FEATURE [PartDesign::Pocket] Pocket007  label="基板部2"
  BaseFeature = -> Pocket001
  Direction = (0,0,-1)
  Length = 4.5
  Length2 = 5
  Profile = -> Sketch018
  ReferenceAxis = -> Sketch018 [N_Axis]
  Refine = true
  Reversed = true
  Suppressed = false
  Type = 0
FEATURE [PartDesign::Pocket] Pocket002  label="電池部"
  BaseFeature = -> Pocket007
  Direction = (0,1,-2e-16)
  Length = 54.1
  Length2 = 5
  Profile = -> Sketch008
  ReferenceAxis = -> Sketch008 [N_Axis]
  Reversed = true
  Suppressed = false
  Type = 0
  expr: Length = Spreadsheet.battery_l + 0.3 * 2 - 3.5
FEATURE [PartDesign::Pocket] Pocket004  label="コネクタ部"
  BaseFeature = -> Pocket002
  Direction = (0,1,-2e-16)
  Length = 5
  Length2 = 5
  Profile = -> Sketch011
  ReferenceAxis = -> Sketch011 [N_Axis]
  Suppressed = false
  Type = 0
FEATURE [PartDesign::Pocket] Pocket006  label="外形カット"
  BaseFeature = -> Pocket004
  Direction = (0,1,-2e-16)
  Length = 100
  Length2 = 100
  Profile = -> Sketch016
  ReferenceAxis = -> Sketch016 [N_Axis]
  Reversed = true
  Suppressed = false
  Type = 4
FEATURE [PartDesign::Fillet] Fillet001
  Base = -> Pocket006 [Edge7,Face1,Edge12,Edge17,Edge22,Edge66,Edge25,Edge24,Edge31,Edge13,Edge18]
  BaseFeature = -> Pocket006
  Radius = 1
  Refine = true
  SupportTransform = false
  Suppressed = false
  UseAllEdges = false
FEATURE [PartDesign::Pad] Pad005  label="固定柱1"
  BaseFeature = -> Fillet001
  Direction = (0,0,1)
  Length = 10
  Length2 = 2.1
  Profile = -> Sketch012
  ReferenceAxis = -> Sketch012 [N_Axis]
  Suppressed = false
  Type = 4
FEATURE [PartDesign::Pad] Pad006  label="固定柱2"
  BaseFeature = -> Pad005
  Direction = (0,0,1)
  Length = 4.5
  Length2 = 10
  Profile = -> Sketch014
  ReferenceAxis = -> Sketch014 [N_Axis]
  Suppressed = false
  Type = 0
FEATURE [PartDesign::Chamfer] Chamfer001  label="固定柱面取り"
  Angle = 45
  Base = -> Pad006 [Face68]
  BaseFeature = -> Pad006
  ChamferType = 0
  FlipDirection = false
  Size = 0.5
  Size2 = 1
  SupportTransform = false
  Suppressed = false
  UseAllEdges = false
FEATURE [PartDesign::Pocket] Pocket005  label="電池ピン穴"
  BaseFeature = -> Chamfer001
  Direction = (0,0,-1)
  Length = 2.2
  Length2 = 5
  Profile = -> Sketch013
  ReferenceAxis = -> Sketch013 [N_Axis]
  Reversed = true
  Suppressed = false
  Type = 0
FEATURE [Sketcher::SketchObject] Sketch019
  ArcFitTolerance = 1e-06
  AttachmentOffset = pos=(0,0,-1.6) rot=(0,0,1;0rad)
  AttachmentSupport = -> [XY_Plane]
  FullyConstrained = false
  MakeInternals = false
  MapMode = 5
  Placement = pos=(0,0,-1.6) rot=(0,0,1;0rad)
  expr: Constraints[10] = Sketch017.Constraints[10]
  expr: Constraints[12] = Sketch017.Constraints[12]
  expr: Constraints[22] = Sketch017.Constraints[22]
  expr: Constraints[23] = Sketch017.Constraints[23]
  expr: Constraints[24] = Sketch017.Constraints[24]
  expr: Constraints[31] = Sketch017.Constraints[31]
  expr: Constraints[42] = Sketch017.Constraints[42]
  expr: Constraints[43] = Sketch017.Constraints[43]
  expr: Constraints[44] = Sketch017.Constraints[44]
  expr: Constraints[45] = Sketch017.Constraints[45]
  expr: Constraints[54] = Sketch017.Constraints[54]
  expr: Constraints[55] = Sketch017.Constraints[55]
  expr: Constraints[56] = Sketch017.Constraints[56]
  expr: Constraints[57] = Sketch017.Constraints[57]
  expr: Constraints[75] = Sketch017.Constraints[75]
  expr: Constraints[76] = Sketch017.Constraints[76]
  expr: Constraints[77] = Sketch017.Constraints[77]
  expr: Constraints[78] = Sketch017.Constraints[78]
  sketch-geometry (30):
    g0: LineSegment [constr] StartX=8.4 StartY=-34 StartZ=0 EndX=8.4 EndY=0 EndZ=0
    g1: LineSegment [constr] StartX=8.4 StartY=0 StartZ=0 EndX=-8.4 EndY=0 EndZ=0
    g2: LineSegment [constr] StartX=-8.4 StartY=0 StartZ=0 EndX=-8.4 EndY=-34 EndZ=0
    g3: LineSegment [constr] StartX=-8.4 StartY=-34 StartZ=0 EndX=8.4 EndY=-34 EndZ=0
    g4: GeomPoint [constr] X=0 Y=-17 Z=0
    g5: LineSegment [constr] StartX=-22.1 StartY=-60.7 StartZ=0 EndX=-22.1 EndY=-3.7 EndZ=0
    g6: LineSegment [constr] StartX=-22.1 StartY=-3.7 StartZ=0 EndX=-9.1 EndY=-3.7 EndZ=0
    g7: LineSegment [constr] StartX=-9.1 StartY=-3.7 StartZ=0 EndX=-9.1 EndY=-60.7 EndZ=0
    g8: LineSegment [constr] StartX=-9.1 StartY=-60.7 StartZ=0 EndX=-22.1 EndY=-60.7 EndZ=0
    g9: GeomPoint [constr] X=-15.6 Y=-32.2 Z=0
    g10: LineSegment [constr] StartX=21.5 StartY=-68.9 StartZ=0 EndX=21.5 EndY=0 EndZ=0
    g11: LineSegment [constr] StartX=21.5 StartY=0 StartZ=0 EndX=-21.5 EndY=0 EndZ=0
    g12: GeomPoint [constr] X=0 Y=-34.45 Z=0
    g13: LineSegment [constr] StartX=8.5 StartY=-53.9 StartZ=0 EndX=8.5 EndY=-36.9 EndZ=0
    g14: LineSegment [constr] StartX=8.5 StartY=-36.9 StartZ=0 EndX=-8.5 EndY=-36.9 EndZ=0
    g15: LineSegment [constr] StartX=-8.5 StartY=-36.9 StartZ=0 EndX=-8.5 EndY=-53.9 EndZ=0
    g16: LineSegment [constr] StartX=-8.5 StartY=-53.9 StartZ=0 EndX=8.5 EndY=-53.9 EndZ=0
    g17: GeomPoint [constr] X=0 Y=-45.4 Z=0
    g18: LineSegment [constr] StartX=-18.1 StartY=-59.7 StartZ=0 EndX=-24.1 EndY=-59.7 EndZ=0
    g19: LineSegment [constr] StartX=-24.1 StartY=-59.7 StartZ=0 EndX=-24.1 EndY=-64.7 EndZ=0
    g20: LineSegment [constr] StartX=-24.1 StartY=-64.7 StartZ=0 EndX=-18.1 EndY=-64.7 EndZ=0
    g21: LineSegment [constr] StartX=-18.1 StartY=-64.7 StartZ=0 EndX=-18.1 EndY=-59.7 EndZ=0
    g22: LineSegment [constr] StartX=-24.1 StartY=-3.3 StartZ=0 EndX=-24.1 EndY=-59.7 EndZ=0
    g23: LineSegment [constr] StartX=-18.1 StartY=-3.3 StartZ=0 EndX=-18.1 EndY=-59.7 EndZ=0
    g24: LineSegment [constr] StartX=-24.1 StartY=-59.7 StartZ=0 EndX=-22.2801 EndY=-64.7 EndZ=0
    g25: LineSegment [constr] StartX=-18.1 StartY=-64.7 StartZ=0 EndX=-22.2801 EndY=-64.7 EndZ=0
    g26: LineSegment StartX=5 StartY=0 StartZ=0 EndX=5 EndY=-1.2 EndZ=0
    g27: LineSegment StartX=5 StartY=-1.2 StartZ=0 EndX=9 EndY=-1.2 EndZ=0
    g28: LineSegment StartX=9 StartY=-1.2 StartZ=0 EndX=9 EndY=0 EndZ=0
    g29: LineSegment StartX=9 StartY=0 StartZ=0 EndX=5 EndY=0 EndZ=0
  constraints (79):
    c: Coincident(g0,g1)
    c: Coincident(g1,g2)
    c: Coincident(g2,g3)
    c: Coincident(g3,g0)
    c: Horizontal(g1)
    c: Horizontal(g3)
    c: Vertical(g0)
    c: Vertical(g2)
    c: Symmetric(g1,g0,g4)
    c: PointOnObject(g4,g-2)
    c: Distance(g0) = 34
    c: PointOnObject(g-1,g1)
    c: Distance(g3) = 16.8
    c: Coincident(g5,g6)
    c: Coincident(g6,g7)
    c: Coincident(g7,g8)
    c: Coincident(g8,g5)
    c: Horizontal(g6)
    c: Horizontal(g8)
    c: Vertical(g5)
    c: Vertical(g7)
    c: Symmetric(g6,g5,g9)
    c: Distance(g6) = 13
    c: Distance(g5) = 57
    c: Distance(g9,g-1) = 32.2
    c: Coincident(g10,g11)
    c: Horizontal(g11)
    c: Vertical(g10)
    c: Symmetric(g11,g10,g12)
    c: PointOnObject(g12,g-2)
    c: PointOnObject(g11,g-1)
    c: Distance(g10) = 68.9
    c: Coincident(g13,g14)
    c: Coincident(g14,g15)
    c: Coincident(g15,g16)
    c: Coincident(g16,g13)
    c: Horizontal(g14)
    c: Horizontal(g16)
    c: Vertical(g13)
    c: Vertical(g15)
    c: Symmetric(g14,g13,g17)
    c: PointOnObject(g17,g-2)
    c: Distance(g16) = 17
    c: Distance(g13) = 17
    c: Distance(g17,g-1) = 45.4
    c: Distance(g9,g-2) = 15.6
    c: Coincident(g18,g19)
    c: Coincident(g19,g20)
    c: Coincident(g20,g21)
    c: Coincident(g21,g18)
    c: Horizontal(g18)
    c: Horizontal(g20)
    c: Vertical(g19)
    c: Vertical(g21)
    c: Distance(g18,g8) = 1
    c: Distance(g19) = 5
    c: Distance(g20) = 6
    c: Distance(g20,g-2) = 18.1
    c: Coincident(g22,g18)
    c: Vertical(g22)
    c: Coincident(g23,g18)
    c: Vertical(g23)
    c: Coincident(g24,g18)
    c: PointOnObject(g24,g20)
    c: Coincident(g25,g20)
    c: Coincident(g25,g24)
    c: Coincident(g26,g27)
    c: Coincident(g27,g28)
    c: Coincident(g28,g29)
    c: Coincident(g29,g26)
    c: Vertical(g26)
    c: Vertical(g28)
    c: Horizontal(g27)
    c: Horizontal(g29)
    c: PointOnObject(g26,g1)
    c: DistanceX(g27,g27) = 4
    c: DistanceY(g28,g28) = 1.2
    c: DistanceX(g-1,g26) = 5
    c: Angle(g25,g24) = 1.91986
FEATURE [PartDesign::Pad] Pad009
  BaseFeature = -> Pocket005
  Direction = (0,0,1)
  Length = 2.3
  Length2 = 10
  Profile = -> Sketch019
  ReferenceAxis = -> Sketch019 [N_Axis]
  Refine = true
  Reversed = true
  Suppressed = false
  Type = 0
FEATURE [PartDesign::Pad] Pad008  label="固定爪1"
  BaseFeature = -> Pad009
  Direction = (0,0,1)
  Length = 2
  Length2 = 10
  Profile = -> Sketch017
  ReferenceAxis = -> Sketch017 [N_Axis]
  Reversed = true
  Suppressed = false
  Type = 0
FEATURE [PartDesign::Chamfer] Chamfer  label="固定爪1_逃げ"
  Angle = 45
  Base = -> Pad008 [Edge244]
  BaseFeature = -> Pad008
  ChamferType = 0
  FlipDirection = false
  Size = 0.9
  Size2 = 1
  SupportTransform = false
  Suppressed = false
  UseAllEdges = false
FEATURE [PartDesign::Body] Body
  AllowCompound = false
  Group = -> [Sketch,Sketch001,Sketch002,Pad,Sketch003,Pocket,Sketch007,Pocket001,Sketch008,Sketch018,Pocket007,Pocket002,Sketch011,Pocket004,Pocket006,Sketch012,Fillet001,Pad005,Sketch013,Sketch014,Pad006,Chamfer001,Pocket005,Sketch016,Sketch017,Sketch019,Pad009,Pad008,Chamfer]
  Origin = -> Origin
  Tip = -> Chamfer
COMPONENT P1 — recipe-attached ("Body003", modeled in this document).
Construction recipe (the document's own serialized feature program — sketch geometry with constraints, then the solid features built on it; lengths are millimeters unless a unit is written):

FEATURE [PartDesign::AdditiveSphere] Sphere
  Angle1 = -90
  Angle2 = 90
  Angle3 = 360
  AttacherType = Attacher::AttachEngine3D
  Radius = 12.5
  Refine = true
  Suppressed = false
FEATURE [PartDesign::Body] Body003
  AllowCompound = false
  Group = -> [Sphere]
  Origin = -> Origin006
  Placement = pos=(37,-63.6,8.7) rot=(0,0,1;0rad)
  Tip = -> Sphere
